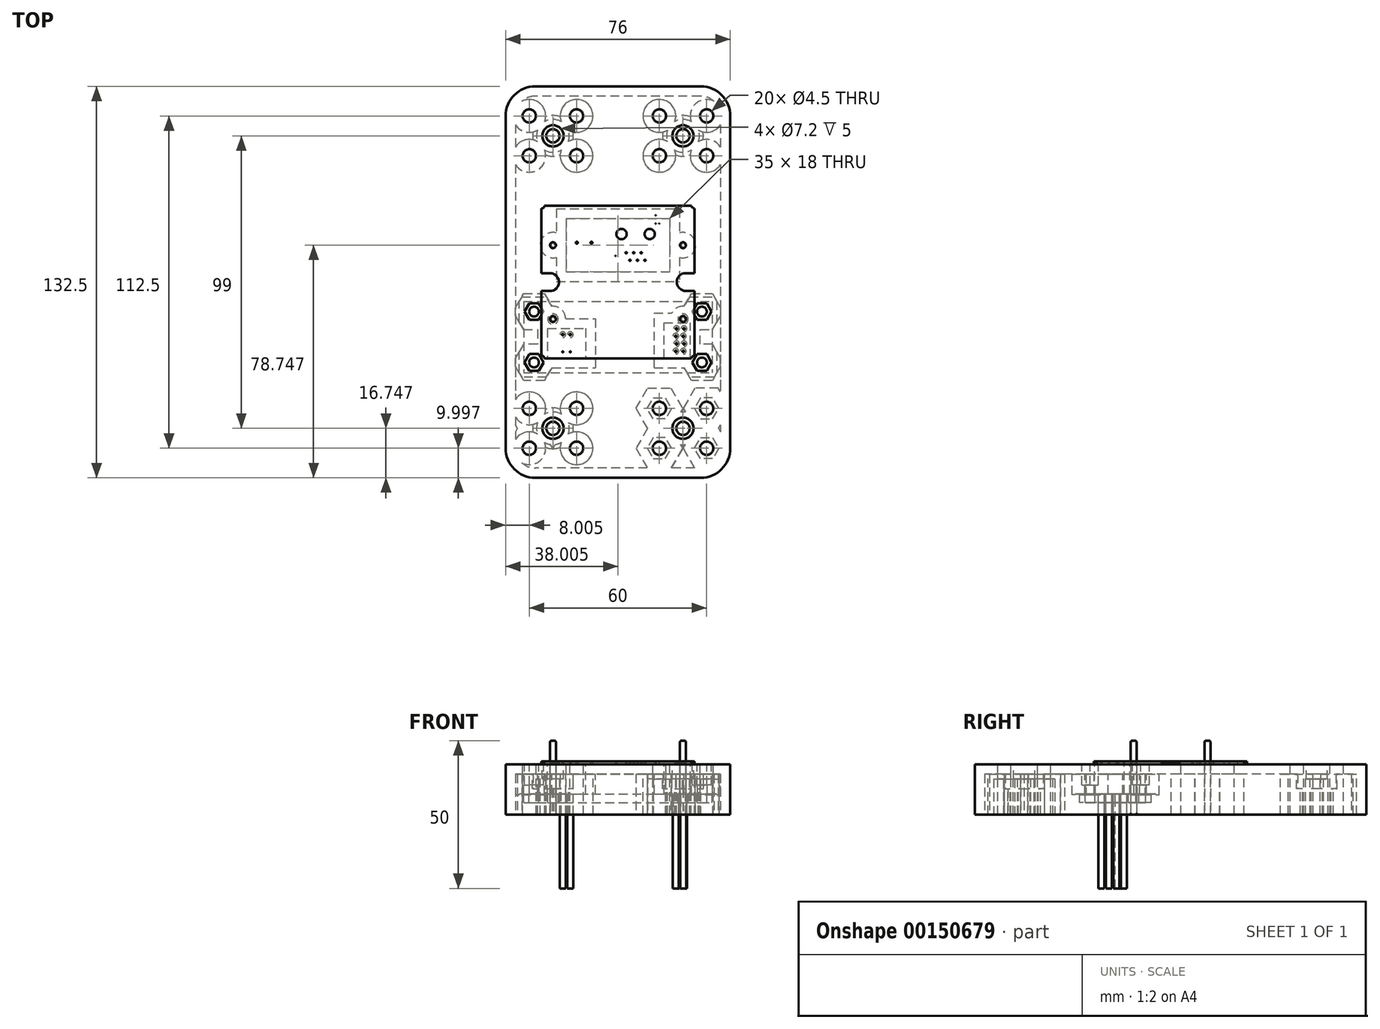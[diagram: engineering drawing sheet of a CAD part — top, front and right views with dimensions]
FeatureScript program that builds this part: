
annotation { "Feature Type Name" : "Feature", "Feature Type Description" : "" }
export const myFeature = defineFeature(function(context is Context, id is Id, definition is map)
    precondition{}
    {
        {
            var Q0;
            Q0=qCreatedBy(makeId("Top.planeOp"),FACE);
            var sketch = newSketch(context, id + "F0", { "sketchPlane" : qUnion([Q0])});
            skLineSegment(sketch, "E0", {"start": v(-14.15, 11.03) * mm, "end": v(-14.15, 0.89) * mm, "construction": true});
            skLineSegment(sketch, "E1", {"start": v(-14.15, 0.89) * mm, "end": v(-9.07, 0.89) * mm, "construction": true});
            skLineSegment(sketch, "E2", {"start": v(-9.07, 0.89) * mm, "end": v(-9.07, 11.03) * mm, "construction": true});
            skLineSegment(sketch, "E3", {"start": v(-9.07, 11.03) * mm, "end": v(-14.15, 11.03) * mm, "construction": true});
            skArc(sketch, "E4", {"start": v(-10.46, 10) * mm, "mid": v(-10.71, 9.75) * mm, "end": v(-10.46, 9.5) * mm});
            skArc(sketch, "E5", {"start": v(-10.46, 9.5) * mm, "mid": v(-10.21, 9.75) * mm, "end": v(-10.46, 10) * mm});
            skArc(sketch, "E6", {"start": v(-13, 10) * mm, "mid": v(-13.25, 9.75) * mm, "end": v(-13, 9.5) * mm});
            skArc(sketch, "E7", {"start": v(-13, 9.5) * mm, "mid": v(-12.75, 9.75) * mm, "end": v(-13, 10) * mm});
            skArc(sketch, "E8", {"start": v(-10.2, 7.46) * mm, "mid": v(-10.46, 7.2) * mm, "end": v(-10.2, 6.96) * mm});
            skArc(sketch, "E9", {"start": v(-10.2, 6.96) * mm, "mid": v(-9.96, 7.2) * mm, "end": v(-10.2, 7.46) * mm});
            skArc(sketch, "E10", {"start": v(-12.75, 7.46) * mm, "mid": v(-13, 7.2) * mm, "end": v(-12.75, 6.96) * mm});
            skArc(sketch, "E11", {"start": v(-12.75, 6.96) * mm, "mid": v(-12.5, 7.2) * mm, "end": v(-12.75, 7.46) * mm});
            skArc(sketch, "E12", {"start": v(-10.46, 4.42) * mm, "mid": v(-10.21, 4.67) * mm, "end": v(-10.46, 4.92) * mm});
            skArc(sketch, "E13", {"start": v(-10.46, 4.92) * mm, "mid": v(-10.71, 4.67) * mm, "end": v(-10.46, 4.42) * mm});
            skArc(sketch, "E14", {"start": v(-13, 4.92) * mm, "mid": v(-13.25, 4.67) * mm, "end": v(-13, 4.42) * mm});
            skArc(sketch, "E15", {"start": v(-13, 4.42) * mm, "mid": v(-12.75, 4.67) * mm, "end": v(-13, 4.92) * mm});
            skArc(sketch, "E16", {"start": v(-10.2, 2.38) * mm, "mid": v(-10.46, 2.13) * mm, "end": v(-10.2, 1.88) * mm});
            skArc(sketch, "E17", {"start": v(-10.2, 1.88) * mm, "mid": v(-9.96, 2.13) * mm, "end": v(-10.2, 2.38) * mm});
            skArc(sketch, "E18", {"start": v(-12.75, 2.38) * mm, "mid": v(-13, 2.13) * mm, "end": v(-12.75, 1.88) * mm});
            skArc(sketch, "E19", {"start": v(-12.75, 1.88) * mm, "mid": v(-12.5, 2.13) * mm, "end": v(-12.75, 2.38) * mm});
            skLineSegment(sketch, "E20", {"start": v(-49.07, -31) * mm, "end": v(-49.07, -23) * mm, "construction": true});
            skLineSegment(sketch, "E21", {"start": v(-49.07, -23) * mm, "end": v(-38.9, -23) * mm, "construction": true});
            skLineSegment(sketch, "E22", {"start": v(-38.9, -23) * mm, "end": v(-38.9, -31) * mm, "construction": true});
            skLineSegment(sketch, "E23", {"start": v(-38.9, -31) * mm, "end": v(-49.07, -31) * mm, "construction": true});
            skArc(sketch, "E24", {"start": v(-46.8, -27) * mm, "mid": v(-46.47, -27.32) * mm, "end": v(-46.15, -27) * mm});
            skArc(sketch, "E25", {"start": v(-46.15, -27) * mm, "mid": v(-46.47, -26.67) * mm, "end": v(-46.8, -27) * mm});
            skArc(sketch, "E26", {"start": v(-46.47, -25.92) * mm, "mid": v(-47.55, -27) * mm, "end": v(-46.47, -28.08) * mm, "construction": true});
            skArc(sketch, "E27", {"start": v(-46.47, -28.08) * mm, "mid": v(-45.4, -27) * mm, "end": v(-46.47, -25.92) * mm, "construction": true});
            skArc(sketch, "E28", {"start": v(-41.82, -27) * mm, "mid": v(-41.5, -27.32) * mm, "end": v(-41.17, -27) * mm});
            skArc(sketch, "E29", {"start": v(-41.17, -27) * mm, "mid": v(-41.5, -26.67) * mm, "end": v(-41.82, -27) * mm});
            skArc(sketch, "E30", {"start": v(-41.5, -25.92) * mm, "mid": v(-42.58, -27) * mm, "end": v(-41.5, -28.08) * mm, "construction": true});
            skArc(sketch, "E31", {"start": v(-41.5, -28.08) * mm, "mid": v(-40.42, -27) * mm, "end": v(-41.5, -25.92) * mm, "construction": true});
            skLineSegment(sketch, "E32", {"start": v(-47.67, 8.94) * mm, "end": v(-52.24, 8.94) * mm, "construction": true});
            skLineSegment(sketch, "E33", {"start": v(-52.24, 8.94) * mm, "end": v(-52.24, 10.97) * mm, "construction": true});
            skLineSegment(sketch, "E34", {"start": v(-52.24, 10.97) * mm, "end": v(-47.67, 10.97) * mm, "construction": true});
            skLineSegment(sketch, "E35", {"start": v(-47.67, 10.97) * mm, "end": v(-47.67, 8.94) * mm, "construction": true});
            skArc(sketch, "E36", {"start": v(-48.5, 9.96) * mm, "mid": v(-48.68, 10.13) * mm, "end": v(-48.86, 9.96) * mm});
            skArc(sketch, "E37", {"start": v(-48.86, 9.96) * mm, "mid": v(-48.68, 9.78) * mm, "end": v(-48.5, 9.96) * mm});
            skArc(sketch, "E38", {"start": v(-51.05, 9.96) * mm, "mid": v(-51.22, 10.13) * mm, "end": v(-51.4, 9.96) * mm});
            skArc(sketch, "E39", {"start": v(-51.4, 9.96) * mm, "mid": v(-51.22, 9.78) * mm, "end": v(-51.05, 9.96) * mm});
            skArc(sketch, "E40", {"start": v(-54.56, -0.55) * mm, "mid": v(-55.16, -1.16) * mm, "end": v(-54.56, -1.77) * mm});
            skArc(sketch, "E41", {"start": v(-54.56, -1.77) * mm, "mid": v(-53.95, -1.16) * mm, "end": v(-54.56, -0.55) * mm});
            skArc(sketch, "E42", {"start": v(-10.56, -1.77) * mm, "mid": v(-9.95, -1.16) * mm, "end": v(-10.56, -0.55) * mm});
            skArc(sketch, "E43", {"start": v(-10.56, -0.55) * mm, "mid": v(-11.16, -1.16) * mm, "end": v(-10.56, -1.77) * mm});
            skArc(sketch, "E44", {"start": v(-54.56, -26.77) * mm, "mid": v(-53.95, -26.16) * mm, "end": v(-54.56, -25.55) * mm});
            skArc(sketch, "E45", {"start": v(-54.56, -25.55) * mm, "mid": v(-55.16, -26.16) * mm, "end": v(-54.56, -26.77) * mm});
            skArc(sketch, "E46", {"start": v(-10.56, -26.77) * mm, "mid": v(-9.95, -26.16) * mm, "end": v(-10.56, -25.55) * mm});
            skArc(sketch, "E47", {"start": v(-10.56, -25.55) * mm, "mid": v(-11.16, -26.16) * mm, "end": v(-10.56, -26.77) * mm});
            skLineSegment(sketch, "E48", {"start": v(-19.8, -19.76) * mm, "end": v(-33.38, -19.76) * mm, "construction": true});
            skLineSegment(sketch, "E49", {"start": v(-33.38, -19.76) * mm, "end": v(-33.38, -36.27) * mm, "construction": true});
            skLineSegment(sketch, "E50", {"start": v(-33.38, -36.27) * mm, "end": v(-19.8, -36.27) * mm, "construction": true});
            skLineSegment(sketch, "E51", {"start": v(-19.8, -36.27) * mm, "end": v(-19.8, -19.76) * mm, "construction": true});
            skArc(sketch, "E52", {"start": v(-33.38, -36.24) * mm, "mid": v(-33.41, -36.27) * mm, "end": v(-33.38, -36.3) * mm, "construction": true});
            skArc(sketch, "E53", {"start": v(-33.38, -36.3) * mm, "mid": v(-33.35, -36.27) * mm, "end": v(-33.38, -36.24) * mm, "construction": true});
            skArc(sketch, "E54", {"start": v(-19.8, -36.24) * mm, "mid": v(-19.82, -36.27) * mm, "end": v(-19.8, -36.3) * mm});
            skArc(sketch, "E55", {"start": v(-19.8, -36.3) * mm, "mid": v(-19.76, -36.27) * mm, "end": v(-19.8, -36.24) * mm});
            skArc(sketch, "E56", {"start": v(-31.35, -28.16) * mm, "mid": v(-33.1, -29.92) * mm, "end": v(-31.35, -31.68) * mm});
            skArc(sketch, "E57", {"start": v(-31.35, -31.68) * mm, "mid": v(-29.6, -29.92) * mm, "end": v(-31.35, -28.16) * mm});
            skArc(sketch, "E58", {"start": v(-21.82, -28.19) * mm, "mid": v(-23.56, -29.92) * mm, "end": v(-21.82, -31.65) * mm});
            skArc(sketch, "E59", {"start": v(-21.82, -31.65) * mm, "mid": v(-20.1, -29.92) * mm, "end": v(-21.82, -28.19) * mm});
            skLineSegment(sketch, "E60", {"start": v(-33.38, -22.55) * mm, "end": v(-34.59, -22.55) * mm, "construction": true});
            skLineSegment(sketch, "E61", {"start": v(-34.59, -22.55) * mm, "end": v(-34.59, -33.48) * mm, "construction": true});
            skLineSegment(sketch, "E62", {"start": v(-34.59, -33.48) * mm, "end": v(-33.38, -33.48) * mm, "construction": true});
            skLineSegment(sketch, "E63", {"start": v(-33.38, -33.48) * mm, "end": v(-33.38, -22.55) * mm, "construction": true});
            skArc(sketch, "E64", {"start": v(-33.38, -22.52) * mm, "mid": v(-33.41, -22.55) * mm, "end": v(-33.38, -22.58) * mm});
            skArc(sketch, "E65", {"start": v(-33.38, -22.58) * mm, "mid": v(-33.35, -22.55) * mm, "end": v(-33.38, -22.52) * mm});
            skArc(sketch, "E66", {"start": v(-34.59, -33.44) * mm, "mid": v(-34.62, -33.48) * mm, "end": v(-34.59, -33.5) * mm, "construction": true});
            skArc(sketch, "E67", {"start": v(-34.59, -33.5) * mm, "mid": v(-34.56, -33.48) * mm, "end": v(-34.59, -33.44) * mm, "construction": true});
            skArc(sketch, "E68", {"start": v(-33.38, -33.44) * mm, "mid": v(-33.41, -33.48) * mm, "end": v(-33.38, -33.5) * mm, "construction": true});
            skArc(sketch, "E69", {"start": v(-33.38, -33.5) * mm, "mid": v(-33.35, -33.48) * mm, "end": v(-33.38, -33.44) * mm, "construction": true});
            skLineSegment(sketch, "E70", {"start": v(-19.8, -22.55) * mm, "end": v(-18.59, -22.55) * mm, "construction": true});
            skLineSegment(sketch, "E71", {"start": v(-18.59, -22.55) * mm, "end": v(-18.59, -33.48) * mm, "construction": true});
            skLineSegment(sketch, "E72", {"start": v(-18.59, -33.48) * mm, "end": v(-19.8, -33.48) * mm});
            skLineSegment(sketch, "E73", {"start": v(-19.8, -33.48) * mm, "end": v(-19.8, -22.55) * mm, "construction": true});
            skArc(sketch, "E74", {"start": v(-18.59, -33.44) * mm, "mid": v(-18.62, -33.48) * mm, "end": v(-18.59, -33.5) * mm});
            skArc(sketch, "E75", {"start": v(-18.59, -33.5) * mm, "mid": v(-18.55, -33.48) * mm, "end": v(-18.59, -33.44) * mm});
            skArc(sketch, "E76", {"start": v(-19.8, -33.44) * mm, "mid": v(-19.82, -33.48) * mm, "end": v(-19.8, -33.5) * mm});
            skArc(sketch, "E77", {"start": v(-19.8, -33.5) * mm, "mid": v(-19.76, -33.48) * mm, "end": v(-19.8, -33.44) * mm});
            skArc(sketch, "E78", {"start": v(-29.76, -23.34) * mm, "mid": v(-29.99, -23.57) * mm, "end": v(-29.76, -23.8) * mm});
            skArc(sketch, "E79", {"start": v(-29.76, -23.8) * mm, "mid": v(-29.54, -23.57) * mm, "end": v(-29.76, -23.34) * mm});
            skArc(sketch, "E80", {"start": v(-28.5, -21.25) * mm, "mid": v(-28.27, -21.03) * mm, "end": v(-28.5, -20.8) * mm});
            skArc(sketch, "E81", {"start": v(-28.5, -20.8) * mm, "mid": v(-28.72, -21.03) * mm, "end": v(-28.5, -21.25) * mm});
            skArc(sketch, "E82", {"start": v(-27.22, -23.34) * mm, "mid": v(-27.45, -23.57) * mm, "end": v(-27.22, -23.8) * mm});
            skArc(sketch, "E83", {"start": v(-27.22, -23.8) * mm, "mid": v(-27, -23.57) * mm, "end": v(-27.22, -23.34) * mm});
            skArc(sketch, "E84", {"start": v(-25.95, -21.25) * mm, "mid": v(-25.73, -21.03) * mm, "end": v(-25.95, -20.8) * mm});
            skArc(sketch, "E85", {"start": v(-25.95, -20.8) * mm, "mid": v(-26.18, -21.03) * mm, "end": v(-25.95, -21.25) * mm});
            skArc(sketch, "E86", {"start": v(-24.68, -23.34) * mm, "mid": v(-24.9, -23.57) * mm, "end": v(-24.68, -23.8) * mm});
            skArc(sketch, "E87", {"start": v(-24.68, -23.8) * mm, "mid": v(-24.46, -23.57) * mm, "end": v(-24.68, -23.34) * mm});
            skArc(sketch, "E88", {"start": v(-23.41, -21.25) * mm, "mid": v(-23.19, -21.03) * mm, "end": v(-23.41, -20.8) * mm});
            skArc(sketch, "E89", {"start": v(-23.41, -20.8) * mm, "mid": v(-23.64, -21.03) * mm, "end": v(-23.41, -21.25) * mm});
            skLineSegment(sketch, "E90", {"start": v(-52.5, 2.85) * mm, "end": v(-47.41, 2.85) * mm, "construction": true});
            skLineSegment(sketch, "E91", {"start": v(-47.41, 2.85) * mm, "end": v(-47.41, 5.39) * mm, "construction": true});
            skLineSegment(sketch, "E92", {"start": v(-47.41, 5.39) * mm, "end": v(-52.5, 5.39) * mm, "construction": true});
            skLineSegment(sketch, "E93", {"start": v(-52.5, 5.39) * mm, "end": v(-52.5, 2.85) * mm, "construction": true});
            skArc(sketch, "E94", {"start": v(-51.47, 4.12) * mm, "mid": v(-51.22, 3.87) * mm, "end": v(-50.97, 4.12) * mm});
            skArc(sketch, "E95", {"start": v(-50.97, 4.12) * mm, "mid": v(-51.22, 4.37) * mm, "end": v(-51.47, 4.12) * mm});
            skArc(sketch, "E96", {"start": v(-48.93, 4.12) * mm, "mid": v(-48.68, 3.87) * mm, "end": v(-48.43, 4.12) * mm});
            skArc(sketch, "E97", {"start": v(-48.43, 4.12) * mm, "mid": v(-48.68, 4.37) * mm, "end": v(-48.93, 4.12) * mm});
            skArc(sketch, "E98", {"start": v(-58.48, -38.56) * mm, "mid": v(-58.46, -38.59) * mm, "end": v(-58.43, -38.56) * mm});
            skArc(sketch, "E99", {"start": v(-58.43, -38.56) * mm, "mid": v(-58.46, -38.54) * mm, "end": v(-58.48, -38.56) * mm});
            skArc(sketch, "E100", {"start": v(-54.42, -16.46) * mm, "mid": v(-54.4, -16.48) * mm, "end": v(-54.37, -16.46) * mm});
            skArc(sketch, "E101", {"start": v(-54.37, -16.46) * mm, "mid": v(-54.4, -16.43) * mm, "end": v(-54.42, -16.46) * mm});
            skArc(sketch, "E102", {"start": v(-53.92, -16.2) * mm, "mid": v(-53.9, -16.23) * mm, "end": v(-53.87, -16.2) * mm});
            skArc(sketch, "E103", {"start": v(-53.87, -16.2) * mm, "mid": v(-53.9, -16.18) * mm, "end": v(-53.92, -16.2) * mm});
            skArc(sketch, "E104", {"start": v(-53.33, -15.7) * mm, "mid": v(-53.3, -15.72) * mm, "end": v(-53.28, -15.7) * mm});
            skArc(sketch, "E105", {"start": v(-53.28, -15.7) * mm, "mid": v(-53.3, -15.67) * mm, "end": v(-53.33, -15.7) * mm});
            skArc(sketch, "E106", {"start": v(-52.98, -15.19) * mm, "mid": v(-52.95, -15.21) * mm, "end": v(-52.93, -15.19) * mm});
            skArc(sketch, "E107", {"start": v(-52.93, -15.19) * mm, "mid": v(-52.95, -15.16) * mm, "end": v(-52.98, -15.19) * mm});
            skArc(sketch, "E108", {"start": v(-52.72, -14.68) * mm, "mid": v(-52.7, -14.7) * mm, "end": v(-52.67, -14.68) * mm});
            skArc(sketch, "E109", {"start": v(-52.67, -14.68) * mm, "mid": v(-52.7, -14.65) * mm, "end": v(-52.72, -14.68) * mm});
            skArc(sketch, "E110", {"start": v(-52.6, -14.17) * mm, "mid": v(-52.57, -14.2) * mm, "end": v(-52.55, -14.17) * mm});
            skArc(sketch, "E111", {"start": v(-52.55, -14.17) * mm, "mid": v(-52.57, -14.15) * mm, "end": v(-52.6, -14.17) * mm});
            skArc(sketch, "E112", {"start": v(-52.54, -13.66) * mm, "mid": v(-52.52, -13.69) * mm, "end": v(-52.5, -13.66) * mm});
            skArc(sketch, "E113", {"start": v(-52.5, -13.66) * mm, "mid": v(-52.52, -13.64) * mm, "end": v(-52.54, -13.66) * mm});
            skArc(sketch, "E114", {"start": v(-52.6, -13.16) * mm, "mid": v(-52.57, -13.18) * mm, "end": v(-52.55, -13.16) * mm});
            skArc(sketch, "E115", {"start": v(-52.55, -13.16) * mm, "mid": v(-52.57, -13.13) * mm, "end": v(-52.6, -13.16) * mm});
            skArc(sketch, "E116", {"start": v(-52.72, -12.65) * mm, "mid": v(-52.7, -12.67) * mm, "end": v(-52.67, -12.65) * mm});
            skArc(sketch, "E117", {"start": v(-52.67, -12.65) * mm, "mid": v(-52.7, -12.62) * mm, "end": v(-52.72, -12.65) * mm});
            skArc(sketch, "E118", {"start": v(-52.98, -12.14) * mm, "mid": v(-52.95, -12.16) * mm, "end": v(-52.93, -12.14) * mm});
            skArc(sketch, "E119", {"start": v(-52.93, -12.14) * mm, "mid": v(-52.95, -12.11) * mm, "end": v(-52.98, -12.14) * mm});
            skArc(sketch, "E120", {"start": v(-53.3, -11.63) * mm, "mid": v(-53.28, -11.66) * mm, "end": v(-53.26, -11.63) * mm});
            skArc(sketch, "E121", {"start": v(-53.26, -11.63) * mm, "mid": v(-53.28, -11.6) * mm, "end": v(-53.3, -11.63) * mm});
            skArc(sketch, "E122", {"start": v(-53.94, -11.12) * mm, "mid": v(-53.92, -11.15) * mm, "end": v(-53.9, -11.12) * mm});
            skArc(sketch, "E123", {"start": v(-53.9, -11.12) * mm, "mid": v(-53.92, -11.1) * mm, "end": v(-53.94, -11.12) * mm});
            skArc(sketch, "E124", {"start": v(-54.5, -10.84) * mm, "mid": v(-54.48, -10.87) * mm, "end": v(-54.45, -10.84) * mm});
            skArc(sketch, "E125", {"start": v(-54.45, -10.84) * mm, "mid": v(-54.48, -10.82) * mm, "end": v(-54.5, -10.84) * mm});
            skArc(sketch, "E126", {"start": v(-55.11, -10.7) * mm, "mid": v(-55.09, -10.72) * mm, "end": v(-55.06, -10.7) * mm});
            skArc(sketch, "E127", {"start": v(-55.06, -10.7) * mm, "mid": v(-55.09, -10.67) * mm, "end": v(-55.11, -10.7) * mm});
            skArc(sketch, "E128", {"start": v(-55.57, -10.66) * mm, "mid": v(-55.54, -10.69) * mm, "end": v(-55.52, -10.66) * mm});
            skArc(sketch, "E129", {"start": v(-55.52, -10.66) * mm, "mid": v(-55.54, -10.64) * mm, "end": v(-55.57, -10.66) * mm});
            skArc(sketch, "E130", {"start": v(-58.48, 11.24) * mm, "mid": v(-58.46, 11.21) * mm, "end": v(-58.43, 11.24) * mm});
            skArc(sketch, "E131", {"start": v(-58.43, 11.24) * mm, "mid": v(-58.46, 11.26) * mm, "end": v(-58.48, 11.24) * mm});
            skArc(sketch, "E132", {"start": v(-58.44, 11.24) * mm, "mid": v(-58.42, 11.21) * mm, "end": v(-58.4, 11.24) * mm});
            skArc(sketch, "E133", {"start": v(-58.4, 11.24) * mm, "mid": v(-58.42, 11.26) * mm, "end": v(-58.44, 11.24) * mm});
            skArc(sketch, "E134", {"start": v(-58.4, 11.24) * mm, "mid": v(-58.37, 11.22) * mm, "end": v(-58.34, 11.24) * mm});
            skArc(sketch, "E135", {"start": v(-58.34, 11.24) * mm, "mid": v(-58.37, 11.27) * mm, "end": v(-58.4, 11.24) * mm});
            skArc(sketch, "E136", {"start": v(-58.24, 11.26) * mm, "mid": v(-58.22, 11.24) * mm, "end": v(-58.2, 11.26) * mm});
            skArc(sketch, "E137", {"start": v(-58.2, 11.26) * mm, "mid": v(-58.22, 11.29) * mm, "end": v(-58.24, 11.26) * mm});
            skArc(sketch, "E138", {"start": v(-58.2, 11.28) * mm, "mid": v(-58.17, 11.25) * mm, "end": v(-58.14, 11.28) * mm});
            skArc(sketch, "E139", {"start": v(-58.14, 11.28) * mm, "mid": v(-58.17, 11.3) * mm, "end": v(-58.2, 11.28) * mm});
            skArc(sketch, "E140", {"start": v(-58.1, 11.3) * mm, "mid": v(-58.08, 11.28) * mm, "end": v(-58.06, 11.3) * mm});
            skArc(sketch, "E141", {"start": v(-58.06, 11.3) * mm, "mid": v(-58.08, 11.33) * mm, "end": v(-58.1, 11.3) * mm});
            skArc(sketch, "E142", {"start": v(-58, 11.36) * mm, "mid": v(-57.98, 11.33) * mm, "end": v(-57.95, 11.36) * mm});
            skArc(sketch, "E143", {"start": v(-57.95, 11.36) * mm, "mid": v(-57.98, 11.38) * mm, "end": v(-58, 11.36) * mm});
            skArc(sketch, "E144", {"start": v(-57.95, 11.39) * mm, "mid": v(-57.92, 11.36) * mm, "end": v(-57.9, 11.39) * mm});
            skArc(sketch, "E145", {"start": v(-57.9, 11.39) * mm, "mid": v(-57.92, 11.41) * mm, "end": v(-57.95, 11.39) * mm});
            skArc(sketch, "E146", {"start": v(-57.9, 11.42) * mm, "mid": v(-57.87, 11.4) * mm, "end": v(-57.85, 11.42) * mm});
            skArc(sketch, "E147", {"start": v(-57.85, 11.42) * mm, "mid": v(-57.87, 11.45) * mm, "end": v(-57.9, 11.42) * mm});
            skArc(sketch, "E148", {"start": v(-57.81, 11.5) * mm, "mid": v(-57.79, 11.47) * mm, "end": v(-57.76, 11.5) * mm});
            skArc(sketch, "E149", {"start": v(-57.76, 11.5) * mm, "mid": v(-57.79, 11.52) * mm, "end": v(-57.81, 11.5) * mm});
            skArc(sketch, "E150", {"start": v(-57.74, 11.56) * mm, "mid": v(-57.72, 11.54) * mm, "end": v(-57.7, 11.56) * mm});
            skArc(sketch, "E151", {"start": v(-57.7, 11.56) * mm, "mid": v(-57.72, 11.59) * mm, "end": v(-57.74, 11.56) * mm});
            skArc(sketch, "E152", {"start": v(-57.68, 11.64) * mm, "mid": v(-57.65, 11.61) * mm, "end": v(-57.63, 11.64) * mm});
            skArc(sketch, "E153", {"start": v(-57.63, 11.64) * mm, "mid": v(-57.65, 11.66) * mm, "end": v(-57.68, 11.64) * mm});
            skArc(sketch, "E154", {"start": v(-57.63, 11.7) * mm, "mid": v(-57.6, 11.68) * mm, "end": v(-57.58, 11.7) * mm});
            skArc(sketch, "E155", {"start": v(-57.58, 11.7) * mm, "mid": v(-57.6, 11.73) * mm, "end": v(-57.63, 11.7) * mm});
            skArc(sketch, "E156", {"start": v(-57.62, 11.73) * mm, "mid": v(-57.6, 11.7) * mm, "end": v(-57.57, 11.73) * mm});
            skArc(sketch, "E157", {"start": v(-57.57, 11.73) * mm, "mid": v(-57.6, 11.76) * mm, "end": v(-57.62, 11.73) * mm});
            skLineSegment(sketch, "E158", {"start": v(-58.46, -38.56) * mm, "end": v(-58.46, -16.66) * mm});
            skLineSegment(sketch, "E159", {"start": v(-58.46, -16.66) * mm, "end": v(-55.47, -16.66) * mm});
            skLineSegment(sketch, "E160", {"start": v(-55.47, -16.66) * mm, "end": v(-54.93, -16.6) * mm});
            skLineSegment(sketch, "E161", {"start": v(-54.93, -16.6) * mm, "end": v(-54.4, -16.46) * mm});
            skLineSegment(sketch, "E162", {"start": v(-54.4, -16.46) * mm, "end": v(-53.9, -16.2) * mm});
            skLineSegment(sketch, "E163", {"start": v(-53.9, -16.2) * mm, "end": v(-53.3, -15.7) * mm});
            skLineSegment(sketch, "E164", {"start": v(-53.3, -15.7) * mm, "end": v(-52.95, -15.19) * mm});
            skLineSegment(sketch, "E165", {"start": v(-52.95, -15.19) * mm, "end": v(-52.7, -14.68) * mm});
            skLineSegment(sketch, "E166", {"start": v(-52.7, -14.68) * mm, "end": v(-52.57, -14.17) * mm});
            skLineSegment(sketch, "E167", {"start": v(-52.57, -14.17) * mm, "end": v(-52.52, -13.66) * mm});
            skLineSegment(sketch, "E168", {"start": v(-52.52, -13.66) * mm, "end": v(-52.57, -13.16) * mm});
            skLineSegment(sketch, "E169", {"start": v(-52.57, -13.16) * mm, "end": v(-52.7, -12.65) * mm});
            skLineSegment(sketch, "E170", {"start": v(-52.7, -12.65) * mm, "end": v(-52.95, -12.14) * mm});
            skLineSegment(sketch, "E171", {"start": v(-52.95, -12.14) * mm, "end": v(-53.28, -11.63) * mm});
            skLineSegment(sketch, "E172", {"start": v(-53.28, -11.63) * mm, "end": v(-53.92, -11.12) * mm});
            skLineSegment(sketch, "E173", {"start": v(-53.92, -11.12) * mm, "end": v(-54.48, -10.84) * mm});
            skLineSegment(sketch, "E174", {"start": v(-54.48, -10.84) * mm, "end": v(-55.09, -10.7) * mm});
            skLineSegment(sketch, "E175", {"start": v(-55.09, -10.7) * mm, "end": v(-55.54, -10.66) * mm});
            skLineSegment(sketch, "E176", {"start": v(-55.54, -10.66) * mm, "end": v(-58.46, -10.66) * mm});
            skLineSegment(sketch, "E177", {"start": v(-58.46, -10.66) * mm, "end": v(-58.46, 11.24) * mm});
            skLineSegment(sketch, "E178", {"start": v(-58.46, 11.24) * mm, "end": v(-58.42, 11.24) * mm});
            skLineSegment(sketch, "E179", {"start": v(-58.42, 11.24) * mm, "end": v(-58.37, 11.24) * mm});
            skLineSegment(sketch, "E180", {"start": v(-58.37, 11.24) * mm, "end": v(-58.22, 11.26) * mm});
            skLineSegment(sketch, "E181", {"start": v(-58.22, 11.26) * mm, "end": v(-58.17, 11.28) * mm});
            skLineSegment(sketch, "E182", {"start": v(-58.17, 11.28) * mm, "end": v(-58.08, 11.3) * mm});
            skLineSegment(sketch, "E183", {"start": v(-58.08, 11.3) * mm, "end": v(-57.98, 11.36) * mm});
            skLineSegment(sketch, "E184", {"start": v(-57.98, 11.36) * mm, "end": v(-57.92, 11.39) * mm});
            skLineSegment(sketch, "E185", {"start": v(-57.92, 11.39) * mm, "end": v(-57.87, 11.42) * mm});
            skLineSegment(sketch, "E186", {"start": v(-57.87, 11.42) * mm, "end": v(-57.79, 11.5) * mm});
            skLineSegment(sketch, "E187", {"start": v(-57.79, 11.5) * mm, "end": v(-57.72, 11.56) * mm});
            skLineSegment(sketch, "E188", {"start": v(-57.72, 11.56) * mm, "end": v(-57.65, 11.64) * mm});
            skLineSegment(sketch, "E189", {"start": v(-57.65, 11.64) * mm, "end": v(-57.6, 11.7) * mm});
            skLineSegment(sketch, "E190", {"start": v(-57.6, 11.7) * mm, "end": v(-57.6, 11.73) * mm});
            skLineSegment(sketch, "E191", {"start": v(-57.6, 11.73) * mm, "end": v(-57.57, 11.77) * mm});
            skLineSegment(sketch, "E192", {"start": v(-57.57, 11.77) * mm, "end": v(-57.52, 11.88) * mm});
            skLineSegment(sketch, "E193", {"start": v(-57.52, 11.88) * mm, "end": v(-57.51, 11.9) * mm});
            skLineSegment(sketch, "E194", {"start": v(-57.51, 11.9) * mm, "end": v(-57.5, 11.94) * mm});
            skLineSegment(sketch, "E195", {"start": v(-57.5, 11.94) * mm, "end": v(-57.49, 11.98) * mm});
            skLineSegment(sketch, "E196", {"start": v(-57.49, 11.98) * mm, "end": v(-57.46, 12.15) * mm});
            skLineSegment(sketch, "E197", {"start": v(-57.46, 12.15) * mm, "end": v(-57.46, 12.2) * mm});
            skLineSegment(sketch, "E198", {"start": v(-57.46, 12.2) * mm, "end": v(-57.46, 12.24) * mm});
            skLineSegment(sketch, "E199", {"start": v(-57.46, 12.24) * mm, "end": v(-7.66, 12.24) * mm});
            skLineSegment(sketch, "E200", {"start": v(-7.66, 12.24) * mm, "end": v(-7.66, 12.22) * mm});
            skLineSegment(sketch, "E201", {"start": v(-7.66, 12.22) * mm, "end": v(-7.64, 12.09) * mm});
            skLineSegment(sketch, "E202", {"start": v(-7.64, 12.09) * mm, "end": v(-7.63, 12.02) * mm});
            skLineSegment(sketch, "E203", {"start": v(-7.63, 12.02) * mm, "end": v(-7.58, 11.85) * mm});
            skLineSegment(sketch, "E204", {"start": v(-7.58, 11.85) * mm, "end": v(-7.54, 11.76) * mm});
            skLineSegment(sketch, "E205", {"start": v(-7.54, 11.76) * mm, "end": v(-7.43, 11.6) * mm});
            skLineSegment(sketch, "E206", {"start": v(-7.43, 11.6) * mm, "end": v(-7.28, 11.46) * mm});
            skLineSegment(sketch, "E207", {"start": v(-7.28, 11.46) * mm, "end": v(-7.11, 11.35) * mm});
            skLineSegment(sketch, "E208", {"start": v(-7.11, 11.35) * mm, "end": v(-6.94, 11.28) * mm});
            skLineSegment(sketch, "E209", {"start": v(-6.94, 11.28) * mm, "end": v(-6.75, 11.24) * mm});
            skLineSegment(sketch, "E210", {"start": v(-6.75, 11.24) * mm, "end": v(-6.67, 11.24) * mm});
            skLineSegment(sketch, "E211", {"start": v(-6.67, 11.24) * mm, "end": v(-6.66, 11.24) * mm});
            skLineSegment(sketch, "E212", {"start": v(-6.66, 11.24) * mm, "end": v(-6.66, -10.66) * mm});
            skLineSegment(sketch, "E213", {"start": v(-6.66, -10.66) * mm, "end": v(-9.64, -10.66) * mm});
            skLineSegment(sketch, "E214", {"start": v(-9.64, -10.66) * mm, "end": v(-10.23, -10.7) * mm});
            skLineSegment(sketch, "E215", {"start": v(-10.23, -10.7) * mm, "end": v(-10.76, -10.87) * mm});
            skLineSegment(sketch, "E216", {"start": v(-10.76, -10.87) * mm, "end": v(-11.24, -11.12) * mm});
            skLineSegment(sketch, "E217", {"start": v(-11.24, -11.12) * mm, "end": v(-11.85, -11.63) * mm});
            skLineSegment(sketch, "E218", {"start": v(-11.85, -11.63) * mm, "end": v(-12.2, -12.14) * mm});
            skLineSegment(sketch, "E219", {"start": v(-12.2, -12.14) * mm, "end": v(-12.44, -12.65) * mm});
            skLineSegment(sketch, "E220", {"start": v(-12.44, -12.65) * mm, "end": v(-12.6, -13.16) * mm});
            skLineSegment(sketch, "E221", {"start": v(-12.6, -13.16) * mm, "end": v(-12.62, -13.66) * mm});
            skLineSegment(sketch, "E222", {"start": v(-12.62, -13.66) * mm, "end": v(-12.6, -14.17) * mm});
            skLineSegment(sketch, "E223", {"start": v(-12.6, -14.17) * mm, "end": v(-12.44, -14.68) * mm});
            skLineSegment(sketch, "E224", {"start": v(-12.44, -14.68) * mm, "end": v(-12.2, -15.19) * mm});
            skLineSegment(sketch, "E225", {"start": v(-12.2, -15.19) * mm, "end": v(-11.85, -15.7) * mm});
            skLineSegment(sketch, "E226", {"start": v(-11.85, -15.7) * mm, "end": v(-11.27, -16.2) * mm});
            skLineSegment(sketch, "E227", {"start": v(-11.27, -16.2) * mm, "end": v(-10.81, -16.46) * mm});
            skLineSegment(sketch, "E228", {"start": v(-10.81, -16.46) * mm, "end": v(-10.2, -16.63) * mm});
            skLineSegment(sketch, "E229", {"start": v(-10.2, -16.63) * mm, "end": v(-9.64, -16.66) * mm});
            skLineSegment(sketch, "E230", {"start": v(-9.64, -16.66) * mm, "end": v(-6.66, -16.66) * mm});
            skLineSegment(sketch, "E231", {"start": v(-6.66, -16.66) * mm, "end": v(-6.66, -38.56) * mm});
            skLineSegment(sketch, "E232", {"start": v(-6.66, -38.56) * mm, "end": v(-6.9, -38.6) * mm});
            skLineSegment(sketch, "E233", {"start": v(-6.9, -38.6) * mm, "end": v(-7.12, -38.68) * mm});
            skLineSegment(sketch, "E234", {"start": v(-7.12, -38.68) * mm, "end": v(-7.33, -38.82) * mm});
            skLineSegment(sketch, "E235", {"start": v(-7.33, -38.82) * mm, "end": v(-7.48, -39) * mm});
            skLineSegment(sketch, "E236", {"start": v(-7.48, -39) * mm, "end": v(-7.56, -39.15) * mm});
            skLineSegment(sketch, "E237", {"start": v(-7.56, -39.15) * mm, "end": v(-7.62, -39.3) * mm});
            skLineSegment(sketch, "E238", {"start": v(-7.62, -39.3) * mm, "end": v(-7.65, -39.43) * mm});
            skLineSegment(sketch, "E239", {"start": v(-7.65, -39.43) * mm, "end": v(-7.66, -39.56) * mm});
            skLineSegment(sketch, "E240", {"start": v(-7.66, -39.56) * mm, "end": v(-57.46, -39.56) * mm});
            skLineSegment(sketch, "E241", {"start": v(-57.46, -39.56) * mm, "end": v(-57.47, -39.4) * mm});
            skLineSegment(sketch, "E242", {"start": v(-57.47, -39.4) * mm, "end": v(-57.5, -39.25) * mm});
            skLineSegment(sketch, "E243", {"start": v(-57.5, -39.25) * mm, "end": v(-57.6, -39.05) * mm});
            skLineSegment(sketch, "E244", {"start": v(-57.6, -39.05) * mm, "end": v(-57.71, -38.9) * mm});
            skLineSegment(sketch, "E245", {"start": v(-57.71, -38.9) * mm, "end": v(-57.85, -38.77) * mm});
            skLineSegment(sketch, "E246", {"start": v(-57.85, -38.77) * mm, "end": v(-58, -38.67) * mm});
            skLineSegment(sketch, "E247", {"start": v(-58, -38.67) * mm, "end": v(-58.12, -38.62) * mm});
            skLineSegment(sketch, "E248", {"start": v(-58.12, -38.62) * mm, "end": v(-58.25, -38.59) * mm});
            skLineSegment(sketch, "E249", {"start": v(-58.25, -38.59) * mm, "end": v(-58.37, -38.57) * mm});
            skLineSegment(sketch, "E250", {"start": v(-58.37, -38.57) * mm, "end": v(-58.46, -38.56) * mm});
            skArc(sketch, "E251.MirrorCS", {"start": v(-58.06, 13.16) * mm, "mid": v(-58.08, 13.14) * mm, "end": v(-58.1, 13.16) * mm});
            skArc(sketch, "E252.MirrorCS", {"start": v(-58, 13.12) * mm, "mid": v(-57.98, 13.14) * mm, "end": v(-57.95, 13.12) * mm});
            skArc(sketch, "E253.MirrorCS", {"start": v(-57.95, 13.12) * mm, "mid": v(-57.98, 13.1) * mm, "end": v(-58, 13.12) * mm});
            skArc(sketch, "E254.MirrorCS", {"start": v(-57.95, 13.08) * mm, "mid": v(-57.92, 13.1) * mm, "end": v(-57.9, 13.08) * mm});
            skArc(sketch, "E255.MirrorCS", {"start": v(-57.9, 13.08) * mm, "mid": v(-57.92, 13.06) * mm, "end": v(-57.95, 13.08) * mm});
            skArc(sketch, "E256.MirrorCS", {"start": v(-57.9, 13.05) * mm, "mid": v(-57.87, 13.07) * mm, "end": v(-57.85, 13.05) * mm});
            skArc(sketch, "E257.MirrorCS", {"start": v(-58.48, 13.24) * mm, "mid": v(-58.46, 13.26) * mm, "end": v(-58.43, 13.24) * mm});
            skArc(sketch, "E258.MirrorCS", {"start": v(-57.85, 13.05) * mm, "mid": v(-57.87, 13.02) * mm, "end": v(-57.9, 13.05) * mm});
            skLineSegment(sketch, "E259.MirrorCS", {"start": v(-58.46, 13.24) * mm, "end": v(-58.42, 13.24) * mm});
            skArc(sketch, "E260.MirrorCS", {"start": v(-57.81, 12.98) * mm, "mid": v(-57.79, 13) * mm, "end": v(-57.76, 12.98) * mm});
            skArc(sketch, "E261.MirrorCS", {"start": v(-58.43, 13.24) * mm, "mid": v(-58.46, 13.21) * mm, "end": v(-58.48, 13.24) * mm});
            skArc(sketch, "E262.MirrorCS", {"start": v(-57.76, 12.98) * mm, "mid": v(-57.79, 12.96) * mm, "end": v(-57.81, 12.98) * mm});
            skLineSegment(sketch, "E263.MirrorCS", {"start": v(-58.42, 13.24) * mm, "end": v(-58.37, 13.23) * mm});
            skArc(sketch, "E264.MirrorCS", {"start": v(-57.74, 12.9) * mm, "mid": v(-57.72, 12.93) * mm, "end": v(-57.7, 12.9) * mm});
            skArc(sketch, "E265.MirrorCS", {"start": v(-58.44, 13.24) * mm, "mid": v(-58.42, 13.26) * mm, "end": v(-58.4, 13.24) * mm});
            skLineSegment(sketch, "E266.MirrorCS", {"start": v(-58.08, 13.16) * mm, "end": v(-57.98, 13.12) * mm});
            skLineSegment(sketch, "E267.MirrorCS", {"start": v(-58.37, 13.23) * mm, "end": v(-58.22, 13.2) * mm});
            skArc(sketch, "E268.MirrorCS", {"start": v(-57.7, 12.9) * mm, "mid": v(-57.72, 12.88) * mm, "end": v(-57.74, 12.9) * mm});
            skArc(sketch, "E269.MirrorCS", {"start": v(-58.4, 13.24) * mm, "mid": v(-58.42, 13.21) * mm, "end": v(-58.44, 13.24) * mm});
            skLineSegment(sketch, "E270.MirrorCS", {"start": v(-57.98, 13.12) * mm, "end": v(-57.92, 13.08) * mm});
            skLineSegment(sketch, "E271.MirrorCS", {"start": v(-58.22, 13.2) * mm, "end": v(-58.17, 13.2) * mm});
            skArc(sketch, "E272.MirrorCS", {"start": v(-57.68, 12.84) * mm, "mid": v(-57.65, 12.86) * mm, "end": v(-57.63, 12.84) * mm});
            skArc(sketch, "E273.MirrorCS", {"start": v(-57.57, 12.74) * mm, "mid": v(-57.6, 12.72) * mm, "end": v(-57.62, 12.74) * mm});
            skArc(sketch, "E274.MirrorCS", {"start": v(-58.4, 13.23) * mm, "mid": v(-58.37, 13.26) * mm, "end": v(-58.34, 13.23) * mm});
            skLineSegment(sketch, "E275.MirrorCS", {"start": v(-57.92, 13.08) * mm, "end": v(-57.87, 13.05) * mm});
            skLineSegment(sketch, "E276.MirrorCS", {"start": v(-57.6, 12.77) * mm, "end": v(-57.6, 12.74) * mm});
            skLineSegment(sketch, "E277.MirrorCS", {"start": v(-58.17, 13.2) * mm, "end": v(-58.08, 13.16) * mm});
            skArc(sketch, "E278.MirrorCS", {"start": v(-57.63, 12.84) * mm, "mid": v(-57.65, 12.81) * mm, "end": v(-57.68, 12.84) * mm});
            skLineSegment(sketch, "E279.MirrorCS", {"start": v(-57.6, 12.74) * mm, "end": v(-57.57, 12.7) * mm});
            skLineSegment(sketch, "E280.MirrorCS", {"start": v(-57.51, 12.56) * mm, "end": v(-57.5, 12.53) * mm});
            skArc(sketch, "E281.MirrorCS", {"start": v(-58.34, 13.23) * mm, "mid": v(-58.37, 13.2) * mm, "end": v(-58.4, 13.23) * mm});
            skLineSegment(sketch, "E282.MirrorCS", {"start": v(-57.87, 13.05) * mm, "end": v(-57.79, 12.98) * mm});
            skLineSegment(sketch, "E283.MirrorCS", {"start": v(-57.57, 12.7) * mm, "end": v(-57.52, 12.6) * mm});
            skLineSegment(sketch, "E284.MirrorCS", {"start": v(-57.5, 12.53) * mm, "end": v(-57.49, 12.5) * mm});
            skArc(sketch, "E285.MirrorCS", {"start": v(-58.24, 13.2) * mm, "mid": v(-58.22, 13.23) * mm, "end": v(-58.2, 13.2) * mm});
            skArc(sketch, "E286.MirrorCS", {"start": v(-57.63, 12.77) * mm, "mid": v(-57.6, 12.8) * mm, "end": v(-57.58, 12.77) * mm});
            skLineSegment(sketch, "E287.MirrorCS", {"start": v(-57.52, 12.6) * mm, "end": v(-57.51, 12.56) * mm});
            skLineSegment(sketch, "E288.MirrorCS", {"start": v(-57.49, 12.5) * mm, "end": v(-57.46, 12.32) * mm});
            skArc(sketch, "E289.MirrorCS", {"start": v(-58.2, 13.2) * mm, "mid": v(-58.22, 13.18) * mm, "end": v(-58.24, 13.2) * mm});
            skLineSegment(sketch, "E290.MirrorCS", {"start": v(-57.79, 12.98) * mm, "end": v(-57.72, 12.9) * mm});
            skLineSegment(sketch, "E291.MirrorCS", {"start": v(-57.46, 12.32) * mm, "end": v(-57.46, 12.28) * mm});
            skArc(sketch, "E292.MirrorCS", {"start": v(-58.2, 13.2) * mm, "mid": v(-58.17, 13.22) * mm, "end": v(-58.14, 13.2) * mm});
            skArc(sketch, "E293.MirrorCS", {"start": v(-57.58, 12.77) * mm, "mid": v(-57.6, 12.75) * mm, "end": v(-57.63, 12.77) * mm});
            skLineSegment(sketch, "E294.MirrorCS", {"start": v(-57.72, 12.9) * mm, "end": v(-57.65, 12.84) * mm});
            skLineSegment(sketch, "E295.MirrorCS", {"start": v(-57.65, 12.84) * mm, "end": v(-57.6, 12.77) * mm});
            skLineSegment(sketch, "E296.MirrorCS", {"start": v(-57.46, 12.28) * mm, "end": v(-57.46, 12.24) * mm});
            skArc(sketch, "E297.MirrorCS", {"start": v(-58.14, 13.2) * mm, "mid": v(-58.17, 13.17) * mm, "end": v(-58.2, 13.2) * mm});
            skArc(sketch, "E298.MirrorCS", {"start": v(-57.62, 12.74) * mm, "mid": v(-57.6, 12.77) * mm, "end": v(-57.57, 12.74) * mm});
            skArc(sketch, "E299.MirrorCS", {"start": v(-58.1, 13.16) * mm, "mid": v(-58.08, 13.19) * mm, "end": v(-58.06, 13.16) * mm});
            skArc(sketch, "E300.MirrorCS", {"start": v(-52.67, 39.15) * mm, "mid": v(-52.7, 39.13) * mm, "end": v(-52.72, 39.15) * mm});
            skArc(sketch, "E301.MirrorCS", {"start": v(-52.72, 37.12) * mm, "mid": v(-52.7, 37.15) * mm, "end": v(-52.67, 37.12) * mm});
            skArc(sketch, "E302.MirrorCS", {"start": v(-52.6, 38.64) * mm, "mid": v(-52.57, 38.67) * mm, "end": v(-52.55, 38.64) * mm});
            skArc(sketch, "E303.MirrorCS", {"start": v(-52.54, 38.14) * mm, "mid": v(-52.52, 38.16) * mm, "end": v(-52.5, 38.14) * mm});
            skLineSegment(sketch, "E304.MirrorCS", {"start": v(-57.6, 63.53) * mm, "end": v(-57.71, 63.37) * mm});
            skArc(sketch, "E305.MirrorCS", {"start": v(-52.67, 37.12) * mm, "mid": v(-52.7, 37.1) * mm, "end": v(-52.72, 37.12) * mm});
            skArc(sketch, "E306.MirrorCS", {"start": v(-53.3, 36.1) * mm, "mid": v(-53.28, 36.13) * mm, "end": v(-53.26, 36.1) * mm});
            skArc(sketch, "E307.MirrorCS", {"start": v(-52.98, 39.66) * mm, "mid": v(-52.95, 39.69) * mm, "end": v(-52.93, 39.66) * mm});
            skArc(sketch, "E308.MirrorCS", {"start": v(-52.55, 38.64) * mm, "mid": v(-52.57, 38.62) * mm, "end": v(-52.6, 38.64) * mm});
            skArc(sketch, "E309.MirrorCS", {"start": v(-52.5, 38.14) * mm, "mid": v(-52.52, 38.11) * mm, "end": v(-52.54, 38.14) * mm});
            skArc(sketch, "E310.MirrorCS", {"start": v(-52.6, 37.63) * mm, "mid": v(-52.57, 37.65) * mm, "end": v(-52.55, 37.63) * mm});
            skArc(sketch, "E311.MirrorCS", {"start": v(-58.48, 63.04) * mm, "mid": v(-58.46, 63.06) * mm, "end": v(-58.43, 63.04) * mm});
            skLineSegment(sketch, "E312.MirrorCS", {"start": v(-57.71, 63.37) * mm, "end": v(-57.85, 63.24) * mm});
            skArc(sketch, "E313.MirrorCS", {"start": v(-52.98, 36.61) * mm, "mid": v(-52.95, 36.64) * mm, "end": v(-52.93, 36.61) * mm});
            skArc(sketch, "E314.MirrorCS", {"start": v(-52.93, 36.61) * mm, "mid": v(-52.95, 36.59) * mm, "end": v(-52.98, 36.61) * mm});
            skArc(sketch, "E315.MirrorCS", {"start": v(-53.26, 36.1) * mm, "mid": v(-53.28, 36.08) * mm, "end": v(-53.3, 36.1) * mm});
            skArc(sketch, "E316.MirrorCS", {"start": v(-52.93, 39.66) * mm, "mid": v(-52.95, 39.64) * mm, "end": v(-52.98, 39.66) * mm});
            skLineSegment(sketch, "E317.MirrorCS", {"start": v(-57.47, 63.87) * mm, "end": v(-57.5, 63.72) * mm});
            skArc(sketch, "E318.MirrorCS", {"start": v(-52.55, 37.63) * mm, "mid": v(-52.57, 37.6) * mm, "end": v(-52.6, 37.63) * mm});
            skLineSegment(sketch, "E319.MirrorCS", {"start": v(-52.95, 39.66) * mm, "end": v(-52.7, 39.15) * mm});
            skLineSegment(sketch, "E320.MirrorCS", {"start": v(-52.7, 39.15) * mm, "end": v(-52.57, 38.64) * mm});
            skLineSegment(sketch, "E321.MirrorCS", {"start": v(-57.85, 63.24) * mm, "end": v(-58, 63.15) * mm});
            skLineSegment(sketch, "E322.MirrorCS", {"start": v(-52.57, 38.64) * mm, "end": v(-52.52, 38.14) * mm});
            skLineSegment(sketch, "E323.MirrorCS", {"start": v(-52.52, 38.14) * mm, "end": v(-52.57, 37.63) * mm});
            skLineSegment(sketch, "E324.MirrorCS", {"start": v(-52.57, 37.63) * mm, "end": v(-52.7, 37.12) * mm});
            skLineSegment(sketch, "E325.MirrorCS", {"start": v(-58.25, 63.06) * mm, "end": v(-58.37, 63.04) * mm});
            skLineSegment(sketch, "E326.MirrorCS", {"start": v(-52.7, 37.12) * mm, "end": v(-52.95, 36.61) * mm});
            skLineSegment(sketch, "E327.MirrorCS", {"start": v(-52.95, 36.61) * mm, "end": v(-53.28, 36.1) * mm});
            skArc(sketch, "E328.MirrorCS", {"start": v(-52.72, 39.15) * mm, "mid": v(-52.7, 39.18) * mm, "end": v(-52.67, 39.15) * mm});
            skArc(sketch, "E329.MirrorCS", {"start": v(-55.11, 35.17) * mm, "mid": v(-55.09, 35.2) * mm, "end": v(-55.06, 35.17) * mm});
            skLineSegment(sketch, "E330.MirrorCS", {"start": v(-57.46, 64.04) * mm, "end": v(-57.47, 63.87) * mm});
            skArc(sketch, "E331.MirrorCS", {"start": v(-58.43, 63.04) * mm, "mid": v(-58.46, 63.01) * mm, "end": v(-58.48, 63.04) * mm});
            skLineSegment(sketch, "E332.MirrorCS", {"start": v(-57.5, 63.72) * mm, "end": v(-57.6, 63.53) * mm});
            skLineSegment(sketch, "E333.MirrorCS", {"start": v(-58, 63.15) * mm, "end": v(-58.12, 63.1) * mm});
            skLineSegment(sketch, "E334.MirrorCS", {"start": v(-58.12, 63.1) * mm, "end": v(-58.25, 63.06) * mm});
            skLineSegment(sketch, "E335.MirrorCS", {"start": v(-58.37, 63.04) * mm, "end": v(-58.46, 63.04) * mm});
            skArc(sketch, "E336.MirrorCS", {"start": v(-55.06, 35.17) * mm, "mid": v(-55.09, 35.14) * mm, "end": v(-55.11, 35.17) * mm});
            skArc(sketch, "E337.MirrorCS", {"start": v(-53.94, 35.6) * mm, "mid": v(-53.92, 35.62) * mm, "end": v(-53.9, 35.6) * mm});
            skArc(sketch, "E338.MirrorCS", {"start": v(-54.45, 35.32) * mm, "mid": v(-54.48, 35.3) * mm, "end": v(-54.5, 35.32) * mm});
            skArc(sketch, "E339.MirrorCS", {"start": v(-55.57, 35.14) * mm, "mid": v(-55.54, 35.16) * mm, "end": v(-55.52, 35.14) * mm});
            skArc(sketch, "E340.MirrorCS", {"start": v(-53.33, 40.17) * mm, "mid": v(-53.3, 40.2) * mm, "end": v(-53.28, 40.17) * mm});
            skLineSegment(sketch, "E341.MirrorCS", {"start": v(-7.66, 12.24) * mm, "end": v(-7.66, 12.25) * mm});
            skArc(sketch, "E342.MirrorCS", {"start": v(-53.9, 35.6) * mm, "mid": v(-53.92, 35.57) * mm, "end": v(-53.94, 35.6) * mm});
            skLineSegment(sketch, "E343.MirrorCS", {"start": v(-53.92, 35.6) * mm, "end": v(-54.48, 35.32) * mm});
            skLineSegment(sketch, "E344.MirrorCS", {"start": v(-54.48, 35.32) * mm, "end": v(-55.09, 35.17) * mm});
            skLineSegment(sketch, "E345.MirrorCS", {"start": v(-55.09, 35.17) * mm, "end": v(-55.54, 35.14) * mm});
            skArc(sketch, "E346.MirrorCS", {"start": v(-55.52, 35.14) * mm, "mid": v(-55.54, 35.11) * mm, "end": v(-55.57, 35.14) * mm});
            skLineSegment(sketch, "E347.MirrorCS", {"start": v(-53.3, 40.17) * mm, "end": v(-52.95, 39.66) * mm});
            skArc(sketch, "E348.MirrorCS", {"start": v(-53.28, 40.17) * mm, "mid": v(-53.3, 40.14) * mm, "end": v(-53.33, 40.17) * mm});
            skLineSegment(sketch, "E349.MirrorCS", {"start": v(-7.66, 12.25) * mm, "end": v(-7.64, 12.39) * mm});
            skArc(sketch, "E350.MirrorCS", {"start": v(-54.5, 35.32) * mm, "mid": v(-54.48, 35.34) * mm, "end": v(-54.45, 35.32) * mm});
            skLineSegment(sketch, "E351.MirrorCS", {"start": v(-53.28, 36.1) * mm, "end": v(-53.92, 35.6) * mm});
            skLineSegment(sketch, "E352.MirrorCS", {"start": v(-7.43, 12.87) * mm, "end": v(-7.28, 13.02) * mm});
            skLineSegment(sketch, "E353.MirrorCS", {"start": v(-7.64, 12.39) * mm, "end": v(-7.63, 12.46) * mm});
            skLineSegment(sketch, "E354.MirrorCS", {"start": v(-7.28, 13.02) * mm, "end": v(-7.11, 13.13) * mm});
            skLineSegment(sketch, "E355.MirrorCS", {"start": v(-6.94, 13.2) * mm, "end": v(-6.75, 13.23) * mm});
            skLineSegment(sketch, "E356.MirrorCS", {"start": v(-7.63, 12.46) * mm, "end": v(-7.58, 12.62) * mm});
            skLineSegment(sketch, "E357.MirrorCS", {"start": v(-7.54, 12.7) * mm, "end": v(-7.43, 12.87) * mm});
            skLineSegment(sketch, "E358.MirrorCS", {"start": v(-7.56, 63.62) * mm, "end": v(-7.62, 63.78) * mm});
            skLineSegment(sketch, "E359.MirrorCS", {"start": v(-7.11, 13.13) * mm, "end": v(-6.94, 13.2) * mm});
            skLineSegment(sketch, "E360.MirrorCS", {"start": v(-6.75, 13.23) * mm, "end": v(-6.67, 13.24) * mm});
            skLineSegment(sketch, "E361.MirrorCS", {"start": v(-6.67, 13.24) * mm, "end": v(-6.66, 13.24) * mm});
            skLineSegment(sketch, "E362.MirrorCS", {"start": v(-7.12, 63.15) * mm, "end": v(-7.33, 63.3) * mm});
            skLineSegment(sketch, "E363.MirrorCS", {"start": v(-7.58, 12.62) * mm, "end": v(-7.54, 12.7) * mm});
            skArc(sketch, "E364.MirrorCS", {"start": v(-19.8, 57.98) * mm, "mid": v(-19.76, 57.95) * mm, "end": v(-19.8, 57.92) * mm});
            skLineSegment(sketch, "E365.MirrorCS", {"start": v(-7.62, 63.78) * mm, "end": v(-7.65, 63.9) * mm});
            skArc(sketch, "E366.MirrorCS", {"start": v(-34.59, 57.92) * mm, "mid": v(-34.62, 57.95) * mm, "end": v(-34.59, 57.98) * mm, "construction": true});
            skArc(sketch, "E367.MirrorCS", {"start": v(-33.38, 60.71) * mm, "mid": v(-33.41, 60.74) * mm, "end": v(-33.38, 60.77) * mm, "construction": true});
            skArc(sketch, "E368.MirrorCS", {"start": v(-54.42, 40.93) * mm, "mid": v(-54.4, 40.96) * mm, "end": v(-54.37, 40.93) * mm});
            skArc(sketch, "E369.MirrorCS", {"start": v(-19.8, 60.71) * mm, "mid": v(-19.82, 60.74) * mm, "end": v(-19.8, 60.77) * mm});
            skArc(sketch, "E370.MirrorCS", {"start": v(-53.92, 40.68) * mm, "mid": v(-53.9, 40.7) * mm, "end": v(-53.87, 40.68) * mm});
            skArc(sketch, "E371.MirrorCS", {"start": v(-18.59, 57.92) * mm, "mid": v(-18.62, 57.95) * mm, "end": v(-18.59, 57.98) * mm});
            skLineSegment(sketch, "E372.MirrorCS", {"start": v(-7.33, 63.3) * mm, "end": v(-7.48, 63.47) * mm});
            skLineSegment(sketch, "E373.MirrorCS", {"start": v(-34.59, 57.95) * mm, "end": v(-33.38, 57.95) * mm, "construction": true});
            skLineSegment(sketch, "E374.MirrorCS", {"start": v(-7.65, 63.9) * mm, "end": v(-7.66, 64.04) * mm});
            skLineSegment(sketch, "E375.MirrorCS", {"start": v(-55.47, 41.14) * mm, "end": v(-54.93, 41.08) * mm});
            skArc(sketch, "E376.MirrorCS", {"start": v(-33.38, 47) * mm, "mid": v(-33.41, 47.03) * mm, "end": v(-33.38, 47.06) * mm});
            skLineSegment(sketch, "E377.MirrorCS", {"start": v(-54.93, 41.08) * mm, "end": v(-54.4, 40.93) * mm});
            skLineSegment(sketch, "E378.MirrorCS", {"start": v(-54.4, 40.93) * mm, "end": v(-53.9, 40.68) * mm});
            skArc(sketch, "E379.MirrorCS", {"start": v(-34.59, 57.98) * mm, "mid": v(-34.56, 57.95) * mm, "end": v(-34.59, 57.92) * mm, "construction": true});
            skLineSegment(sketch, "E380.MirrorCS", {"start": v(-53.9, 40.68) * mm, "end": v(-53.3, 40.17) * mm});
            skArc(sketch, "E381.MirrorCS", {"start": v(-33.38, 57.92) * mm, "mid": v(-33.41, 57.95) * mm, "end": v(-33.38, 57.98) * mm, "construction": true});
            skArc(sketch, "E382.MirrorCS", {"start": v(-33.38, 57.98) * mm, "mid": v(-33.35, 57.95) * mm, "end": v(-33.38, 57.92) * mm, "construction": true});
            skArc(sketch, "E383.MirrorCS", {"start": v(-33.38, 60.77) * mm, "mid": v(-33.35, 60.74) * mm, "end": v(-33.38, 60.71) * mm, "construction": true});
            skArc(sketch, "E384.MirrorCS", {"start": v(-54.37, 40.93) * mm, "mid": v(-54.4, 40.9) * mm, "end": v(-54.42, 40.93) * mm});
            skArc(sketch, "E385.MirrorCS", {"start": v(-19.8, 60.77) * mm, "mid": v(-19.76, 60.74) * mm, "end": v(-19.8, 60.71) * mm});
            skArc(sketch, "E386.MirrorCS", {"start": v(-53.87, 40.68) * mm, "mid": v(-53.9, 40.65) * mm, "end": v(-53.92, 40.68) * mm});
            skLineSegment(sketch, "E387.MirrorCS", {"start": v(-18.59, 57.95) * mm, "end": v(-19.8, 57.95) * mm});
            skLineSegment(sketch, "E388.MirrorCS", {"start": v(-6.66, 63.04) * mm, "end": v(-6.9, 63.07) * mm});
            skLineSegment(sketch, "E389.MirrorCS", {"start": v(-6.9, 63.07) * mm, "end": v(-7.12, 63.15) * mm});
            skArc(sketch, "E390.MirrorCS", {"start": v(-18.59, 57.98) * mm, "mid": v(-18.55, 57.95) * mm, "end": v(-18.59, 57.92) * mm});
            skArc(sketch, "E391.MirrorCS", {"start": v(-19.8, 57.92) * mm, "mid": v(-19.82, 57.95) * mm, "end": v(-19.8, 57.98) * mm});
            skLineSegment(sketch, "E392.MirrorCS", {"start": v(-7.48, 63.47) * mm, "end": v(-7.56, 63.62) * mm});
            skArc(sketch, "E393.MirrorCS", {"start": v(-41.17, 51.47) * mm, "mid": v(-41.5, 51.15) * mm, "end": v(-41.82, 51.47) * mm});
            skArc(sketch, "E394.MirrorCS", {"start": v(-51.47, 20.36) * mm, "mid": v(-51.22, 20.6) * mm, "end": v(-50.97, 20.36) * mm});
            skArc(sketch, "E395.MirrorCS", {"start": v(-48.93, 20.36) * mm, "mid": v(-48.68, 20.6) * mm, "end": v(-48.43, 20.36) * mm});
            skArc(sketch, "E396.MirrorCS", {"start": v(-28.5, 45.73) * mm, "mid": v(-28.27, 45.5) * mm, "end": v(-28.5, 45.28) * mm});
            skArc(sketch, "E397.MirrorCS", {"start": v(-33.38, 47.06) * mm, "mid": v(-33.35, 47.03) * mm, "end": v(-33.38, 47) * mm});
            skArc(sketch, "E398.MirrorCS", {"start": v(-25.95, 45.73) * mm, "mid": v(-25.73, 45.5) * mm, "end": v(-25.95, 45.28) * mm});
            skArc(sketch, "E399.MirrorCS", {"start": v(-48.5, 14.51) * mm, "mid": v(-48.68, 14.34) * mm, "end": v(-48.86, 14.51) * mm});
            skArc(sketch, "E400.MirrorCS", {"start": v(-51.05, 14.51) * mm, "mid": v(-51.22, 14.34) * mm, "end": v(-51.4, 14.51) * mm});
            skArc(sketch, "E401.MirrorCS", {"start": v(-23.41, 45.73) * mm, "mid": v(-23.19, 45.5) * mm, "end": v(-23.41, 45.28) * mm});
            skLineSegment(sketch, "E402.MirrorCS", {"start": v(-52.5, 19.09) * mm, "end": v(-52.5, 21.63) * mm, "construction": true});
            skArc(sketch, "E403.MirrorCS", {"start": v(-41.5, 50.4) * mm, "mid": v(-42.58, 51.47) * mm, "end": v(-41.5, 52.55) * mm, "construction": true});
            skArc(sketch, "E404.MirrorCS", {"start": v(-41.5, 52.55) * mm, "mid": v(-40.42, 51.47) * mm, "end": v(-41.5, 50.4) * mm, "construction": true});
            skArc(sketch, "E405.MirrorCS", {"start": v(-50.97, 20.36) * mm, "mid": v(-51.22, 20.1) * mm, "end": v(-51.47, 20.36) * mm});
            skArc(sketch, "E406.MirrorCS", {"start": v(-10.2, 22.1) * mm, "mid": v(-10.46, 22.35) * mm, "end": v(-10.2, 22.6) * mm});
            skLineSegment(sketch, "E407.MirrorCS", {"start": v(-47.67, 15.53) * mm, "end": v(-52.24, 15.53) * mm, "construction": true});
            skArc(sketch, "E408.MirrorCS", {"start": v(-10.2, 22.6) * mm, "mid": v(-9.96, 22.35) * mm, "end": v(-10.2, 22.1) * mm});
            skArc(sketch, "E409.MirrorCS", {"start": v(-28.5, 45.28) * mm, "mid": v(-28.72, 45.5) * mm, "end": v(-28.5, 45.73) * mm});
            skLineSegment(sketch, "E410.MirrorCS", {"start": v(-52.24, 15.53) * mm, "end": v(-52.24, 13.5) * mm, "construction": true});
            skArc(sketch, "E411.MirrorCS", {"start": v(-48.43, 20.36) * mm, "mid": v(-48.68, 20.1) * mm, "end": v(-48.93, 20.36) * mm});
            skLineSegment(sketch, "E412.MirrorCS", {"start": v(-52.24, 13.5) * mm, "end": v(-47.67, 13.5) * mm, "construction": true});
            skLineSegment(sketch, "E413.MirrorCS", {"start": v(-47.67, 13.5) * mm, "end": v(-47.67, 15.53) * mm, "construction": true});
            skArc(sketch, "E414.MirrorCS", {"start": v(-25.95, 45.28) * mm, "mid": v(-26.18, 45.5) * mm, "end": v(-25.95, 45.73) * mm});
            skArc(sketch, "E415.MirrorCS", {"start": v(-48.86, 14.51) * mm, "mid": v(-48.68, 14.69) * mm, "end": v(-48.5, 14.51) * mm});
            skArc(sketch, "E416.MirrorCS", {"start": v(-51.4, 14.51) * mm, "mid": v(-51.22, 14.69) * mm, "end": v(-51.05, 14.51) * mm});
            skArc(sketch, "E417.MirrorCS", {"start": v(-46.8, 51.47) * mm, "mid": v(-46.47, 51.8) * mm, "end": v(-46.15, 51.47) * mm});
            skArc(sketch, "E418.MirrorCS", {"start": v(-46.15, 51.47) * mm, "mid": v(-46.47, 51.15) * mm, "end": v(-46.8, 51.47) * mm});
            skArc(sketch, "E419.MirrorCS", {"start": v(-23.41, 45.28) * mm, "mid": v(-23.64, 45.5) * mm, "end": v(-23.41, 45.73) * mm});
            skArc(sketch, "E420.MirrorCS", {"start": v(-46.47, 50.4) * mm, "mid": v(-47.55, 51.47) * mm, "end": v(-46.47, 52.55) * mm, "construction": true});
            skLineSegment(sketch, "E421.MirrorCS", {"start": v(-52.5, 21.63) * mm, "end": v(-47.41, 21.63) * mm, "construction": true});
            skArc(sketch, "E422.MirrorCS", {"start": v(-46.47, 52.55) * mm, "mid": v(-45.4, 51.47) * mm, "end": v(-46.47, 50.4) * mm, "construction": true});
            skLineSegment(sketch, "E423.MirrorCS", {"start": v(-47.41, 21.63) * mm, "end": v(-47.41, 19.09) * mm, "construction": true});
            skLineSegment(sketch, "E424.MirrorCS", {"start": v(-33.38, 47.03) * mm, "end": v(-34.59, 47.03) * mm, "construction": true});
            skArc(sketch, "E425.MirrorCS", {"start": v(-41.82, 51.47) * mm, "mid": v(-41.5, 51.8) * mm, "end": v(-41.17, 51.47) * mm});
            skLineSegment(sketch, "E426.MirrorCS", {"start": v(-47.41, 19.09) * mm, "end": v(-52.5, 19.09) * mm, "construction": true});
            skArc(sketch, "E427.MirrorCS", {"start": v(-10.46, 19.56) * mm, "mid": v(-10.71, 19.8) * mm, "end": v(-10.46, 20.06) * mm});
            skArc(sketch, "E428.MirrorCS", {"start": v(-13, 19.56) * mm, "mid": v(-13.25, 19.8) * mm, "end": v(-13, 20.06) * mm});
            skArc(sketch, "E429.MirrorCS", {"start": v(-13, 20.06) * mm, "mid": v(-12.75, 19.8) * mm, "end": v(-13, 19.56) * mm});
            skArc(sketch, "E430.MirrorCS", {"start": v(-10.2, 17.02) * mm, "mid": v(-10.46, 17.27) * mm, "end": v(-10.2, 17.52) * mm});
            skArc(sketch, "E431.MirrorCS", {"start": v(-12.75, 17.02) * mm, "mid": v(-13, 17.27) * mm, "end": v(-12.75, 17.52) * mm});
            skLineSegment(sketch, "E432.MirrorCS", {"start": v(-12.6, 37.63) * mm, "end": v(-12.62, 38.14) * mm});
            skArc(sketch, "E433.MirrorCS", {"start": v(-29.76, 47.82) * mm, "mid": v(-29.99, 48.04) * mm, "end": v(-29.76, 48.27) * mm});
            skLineSegment(sketch, "E434.MirrorCS", {"start": v(-12.44, 39.15) * mm, "end": v(-12.2, 39.66) * mm});
            skArc(sketch, "E435.MirrorCS", {"start": v(-12.75, 22.1) * mm, "mid": v(-13, 22.35) * mm, "end": v(-12.75, 22.6) * mm});
            skArc(sketch, "E436.MirrorCS", {"start": v(-27.22, 47.82) * mm, "mid": v(-27.45, 48.04) * mm, "end": v(-27.22, 48.27) * mm});
            skArc(sketch, "E437.MirrorCS", {"start": v(-27.22, 48.27) * mm, "mid": v(-27, 48.04) * mm, "end": v(-27.22, 47.82) * mm});
            skArc(sketch, "E438.MirrorCS", {"start": v(-13, 14.48) * mm, "mid": v(-13.25, 14.73) * mm, "end": v(-13, 14.98) * mm});
            skArc(sketch, "E439.MirrorCS", {"start": v(-10.2, 17.52) * mm, "mid": v(-9.96, 17.27) * mm, "end": v(-10.2, 17.02) * mm});
            skArc(sketch, "E440.MirrorCS", {"start": v(-12.75, 17.52) * mm, "mid": v(-12.5, 17.27) * mm, "end": v(-12.75, 17.02) * mm});
            skArc(sketch, "E441.MirrorCS", {"start": v(-10.46, 20.06) * mm, "mid": v(-10.21, 19.8) * mm, "end": v(-10.46, 19.56) * mm});
            skArc(sketch, "E442.MirrorCS", {"start": v(-54.56, 50.03) * mm, "mid": v(-55.16, 50.64) * mm, "end": v(-54.56, 51.25) * mm});
            skLineSegment(sketch, "E443.MirrorCS", {"start": v(-12.62, 38.14) * mm, "end": v(-12.6, 38.64) * mm});
            skArc(sketch, "E444.MirrorCS", {"start": v(-29.76, 48.27) * mm, "mid": v(-29.54, 48.04) * mm, "end": v(-29.76, 47.82) * mm});
            skLineSegment(sketch, "E445.MirrorCS", {"start": v(-12.6, 38.64) * mm, "end": v(-12.44, 39.15) * mm});
            skLineSegment(sketch, "E446.MirrorCS", {"start": v(-12.2, 39.66) * mm, "end": v(-11.85, 40.17) * mm});
            skLineSegment(sketch, "E447.MirrorCS", {"start": v(-11.85, 40.17) * mm, "end": v(-11.27, 40.68) * mm});
            skArc(sketch, "E448.MirrorCS", {"start": v(-12.75, 22.6) * mm, "mid": v(-12.5, 22.35) * mm, "end": v(-12.75, 22.1) * mm});
            skLineSegment(sketch, "E449.MirrorCS", {"start": v(-11.27, 40.68) * mm, "end": v(-10.81, 40.93) * mm});
            skLineSegment(sketch, "E450.MirrorCS", {"start": v(-10.81, 40.93) * mm, "end": v(-10.2, 41.1) * mm});
            skArc(sketch, "E451.MirrorCS", {"start": v(-24.68, 47.82) * mm, "mid": v(-24.9, 48.04) * mm, "end": v(-24.68, 48.27) * mm});
            skLineSegment(sketch, "E452.MirrorCS", {"start": v(-9.64, 35.14) * mm, "end": v(-10.23, 35.17) * mm});
            skArc(sketch, "E453.MirrorCS", {"start": v(-24.68, 48.27) * mm, "mid": v(-24.46, 48.04) * mm, "end": v(-24.68, 47.82) * mm});
            skLineSegment(sketch, "E454.MirrorCS", {"start": v(-10.23, 35.17) * mm, "end": v(-10.76, 35.34) * mm});
            skArc(sketch, "E455.MirrorCS", {"start": v(-54.56, 25.03) * mm, "mid": v(-55.16, 25.64) * mm, "end": v(-54.56, 26.25) * mm});
            skLineSegment(sketch, "E456.MirrorCS", {"start": v(-10.76, 35.34) * mm, "end": v(-11.24, 35.6) * mm});
            skArc(sketch, "E457.MirrorCS", {"start": v(-54.56, 26.25) * mm, "mid": v(-53.95, 25.64) * mm, "end": v(-54.56, 25.03) * mm});
            skLineSegment(sketch, "E458.MirrorCS", {"start": v(-11.24, 35.6) * mm, "end": v(-11.85, 36.1) * mm});
            skArc(sketch, "E459.MirrorCS", {"start": v(-10.56, 26.25) * mm, "mid": v(-9.95, 25.64) * mm, "end": v(-10.56, 25.03) * mm});
            skLineSegment(sketch, "E460.MirrorCS", {"start": v(-11.85, 36.1) * mm, "end": v(-12.2, 36.61) * mm});
            skArc(sketch, "E461.MirrorCS", {"start": v(-10.56, 25.03) * mm, "mid": v(-11.16, 25.64) * mm, "end": v(-10.56, 26.25) * mm});
            skLineSegment(sketch, "E462.MirrorCS", {"start": v(-12.2, 36.61) * mm, "end": v(-12.44, 37.12) * mm});
            skArc(sketch, "E463.MirrorCS", {"start": v(-54.56, 51.25) * mm, "mid": v(-53.95, 50.64) * mm, "end": v(-54.56, 50.03) * mm});
            skLineSegment(sketch, "E464.MirrorCS", {"start": v(-12.44, 37.12) * mm, "end": v(-12.6, 37.63) * mm});
            skLineSegment(sketch, "E465.MirrorCS", {"start": v(-14.15, 13.45) * mm, "end": v(-14.15, 23.59) * mm, "construction": true});
            skLineSegment(sketch, "E466.MirrorCS", {"start": v(-14.15, 23.59) * mm, "end": v(-9.07, 23.59) * mm, "construction": true});
            skLineSegment(sketch, "E467.MirrorCS", {"start": v(-9.07, 23.59) * mm, "end": v(-9.07, 13.45) * mm, "construction": true});
            skLineSegment(sketch, "E468.MirrorCS", {"start": v(-9.07, 13.45) * mm, "end": v(-14.15, 13.45) * mm, "construction": true});
            skArc(sketch, "E469.MirrorCS", {"start": v(-10.46, 14.48) * mm, "mid": v(-10.71, 14.73) * mm, "end": v(-10.46, 14.98) * mm});
            skArc(sketch, "E470.MirrorCS", {"start": v(-10.46, 14.98) * mm, "mid": v(-10.21, 14.73) * mm, "end": v(-10.46, 14.48) * mm});
            skArc(sketch, "E471.MirrorCS", {"start": v(-13, 14.98) * mm, "mid": v(-12.75, 14.73) * mm, "end": v(-13, 14.48) * mm});
            skArc(sketch, "E472.MirrorCS", {"start": v(-10.56, 51.25) * mm, "mid": v(-9.95, 50.64) * mm, "end": v(-10.56, 50.03) * mm});
            skArc(sketch, "E473.MirrorCS", {"start": v(-10.56, 50.03) * mm, "mid": v(-11.16, 50.64) * mm, "end": v(-10.56, 51.25) * mm});
            skLineSegment(sketch, "E474.MirrorCS", {"start": v(-58.46, 41.14) * mm, "end": v(-55.47, 41.14) * mm});
            skLineSegment(sketch, "E475.MirrorCS", {"start": v(-55.54, 35.14) * mm, "end": v(-58.46, 35.14) * mm});
            skLineSegment(sketch, "E476.MirrorCS", {"start": v(-6.66, 35.14) * mm, "end": v(-9.64, 35.14) * mm});
            skLineSegment(sketch, "E477.MirrorCS", {"start": v(-10.2, 41.1) * mm, "end": v(-9.64, 41.14) * mm});
            skLineSegment(sketch, "E478.MirrorCS", {"start": v(-19.8, 47.03) * mm, "end": v(-18.59, 47.03) * mm, "construction": true});
            skLineSegment(sketch, "E479.MirrorCS", {"start": v(-9.64, 41.14) * mm, "end": v(-6.66, 41.14) * mm});
            skArc(sketch, "E480.MirrorCS", {"start": v(-31.35, 52.64) * mm, "mid": v(-33.1, 54.4) * mm, "end": v(-31.35, 56.15) * mm});
            skArc(sketch, "E481.MirrorCS", {"start": v(-21.82, 56.13) * mm, "mid": v(-20.1, 54.4) * mm, "end": v(-21.82, 52.66) * mm});
            skLineSegment(sketch, "E482.MirrorCS", {"start": v(-33.38, 57.95) * mm, "end": v(-33.38, 47.03) * mm, "construction": true});
            skLineSegment(sketch, "E483.MirrorCS", {"start": v(-19.8, 60.74) * mm, "end": v(-19.8, 44.23) * mm, "construction": true});
            skLineSegment(sketch, "E484.MirrorCS", {"start": v(-34.59, 47.03) * mm, "end": v(-34.59, 57.95) * mm, "construction": true});
            skLineSegment(sketch, "E485.MirrorCS", {"start": v(-58.46, 63.04) * mm, "end": v(-58.46, 41.14) * mm});
            skLineSegment(sketch, "E486.MirrorCS", {"start": v(-7.66, 64.04) * mm, "end": v(-57.46, 64.04) * mm});
            skLineSegment(sketch, "E487.MirrorCS", {"start": v(-19.8, 44.23) * mm, "end": v(-33.38, 44.23) * mm, "construction": true});
            skLineSegment(sketch, "E488.MirrorCS", {"start": v(-58.46, 35.14) * mm, "end": v(-58.46, 13.24) * mm});
            skLineSegment(sketch, "E489.MirrorCS", {"start": v(-33.38, 44.23) * mm, "end": v(-33.38, 60.74) * mm, "construction": true});
            skLineSegment(sketch, "E490.MirrorCS", {"start": v(-33.38, 60.74) * mm, "end": v(-19.8, 60.74) * mm, "construction": true});
            skLineSegment(sketch, "E491.MirrorCS", {"start": v(-49.07, 55.47) * mm, "end": v(-49.07, 47.47) * mm, "construction": true});
            skLineSegment(sketch, "E492.MirrorCS", {"start": v(-6.66, 13.24) * mm, "end": v(-6.66, 35.14) * mm});
            skLineSegment(sketch, "E493.MirrorCS", {"start": v(-49.07, 47.47) * mm, "end": v(-38.9, 47.47) * mm, "construction": true});
            skLineSegment(sketch, "E494.MirrorCS", {"start": v(-38.9, 47.47) * mm, "end": v(-38.9, 55.47) * mm, "construction": true});
            skLineSegment(sketch, "E495.MirrorCS", {"start": v(-38.9, 55.47) * mm, "end": v(-49.07, 55.47) * mm, "construction": true});
            skLineSegment(sketch, "E496.MirrorCS", {"start": v(-19.8, 57.95) * mm, "end": v(-19.8, 47.03) * mm, "construction": true});
            skLineSegment(sketch, "E497.MirrorCS", {"start": v(-18.59, 47.03) * mm, "end": v(-18.59, 57.95) * mm, "construction": true});
            skLineSegment(sketch, "E498.MirrorCS", {"start": v(-6.66, 41.14) * mm, "end": v(-6.66, 63.04) * mm});
            skArc(sketch, "E499.MirrorCS", {"start": v(-31.35, 56.15) * mm, "mid": v(-29.6, 54.4) * mm, "end": v(-31.35, 52.64) * mm});
            skArc(sketch, "E500.MirrorCS", {"start": v(-21.82, 52.66) * mm, "mid": v(-23.56, 54.4) * mm, "end": v(-21.82, 56.13) * mm});
            skSolve(sketch);
        }
        {
            var Q0;
            Q0=makeQuery(id+"F0.imprint","IMPRINT",FACE,{"disambiguationData":[TD([[makeQuery(id+"F0.imprint","IMPRINT",EDGE,{"derivedFrom":sQuery(id+"F0.wireOp",EDGE,"E199")}),1.0]])]});
            extrude(context, id + "F1", {"entities" : qUnion([Q0]), "depth" : 1 * mm});
        }
        {
            var Q0;
            Q0=qCreatedBy(makeId("Top.planeOp"),FACE);
            var sketch = newSketch(context, id + "F2", { "sketchPlane" : qUnion([Q0])});
            skLineSegment(sketch, "E501.bottom", {"start": v(5.44, 104.39) * mm, "end": v(-70.56, 104.39) * mm});
            skLineSegment(sketch, "E501.top", {"start": v(5.44, -28.11) * mm, "end": v(-70.56, -28.11) * mm});
            skLineSegment(sketch, "E501.left", {"start": v(5.44, 104.39) * mm, "end": v(5.44, -28.11) * mm});
            skLineSegment(sketch, "E501.right", {"start": v(-70.56, 104.39) * mm, "end": v(-70.56, -28.11) * mm});
            skPoint(sketch, "E501.middle", {"position": v(-32.56, 38.14) * mm});
            skLineSegment(sketch, "E502.bottom", {"start": v(-10.56, 50.64) * mm, "end": v(-54.56, 50.64) * mm, "construction": true});
            skLineSegment(sketch, "E502.top", {"start": v(-10.56, 25.64) * mm, "end": v(-54.56, 25.64) * mm, "construction": true});
            skLineSegment(sketch, "E502.left", {"start": v(-10.56, 50.64) * mm, "end": v(-10.56, 25.64) * mm, "construction": true});
            skLineSegment(sketch, "E502.right", {"start": v(-54.56, 50.64) * mm, "end": v(-54.56, 25.64) * mm, "construction": true});
            skLineSegment(sketch, "E503.bottom", {"start": v(-56.46, 22.44) * mm, "end": v(-43.45, 22.44) * mm});
            skLineSegment(sketch, "E503.top", {"start": v(-56.46, 12.43) * mm, "end": v(-43.45, 12.43) * mm});
            skLineSegment(sketch, "E503.left", {"start": v(-56.46, 22.44) * mm, "end": v(-56.46, 12.43) * mm});
            skLineSegment(sketch, "E503.right", {"start": v(-43.45, 22.44) * mm, "end": v(-43.45, 12.43) * mm});
            skPoint(sketch, "E503.middle", {"position": v(-49.95, 17.44) * mm});
            skLineSegment(sketch, "E504.bottom", {"start": v(-50.06, 59.64) * mm, "end": v(-15.06, 59.64) * mm});
            skLineSegment(sketch, "E504.top", {"start": v(-50.06, 41.64) * mm, "end": v(-15.06, 41.64) * mm});
            skLineSegment(sketch, "E504.left", {"start": v(-50.06, 59.64) * mm, "end": v(-50.06, 41.64) * mm});
            skLineSegment(sketch, "E504.right", {"start": v(-15.06, 59.64) * mm, "end": v(-15.06, 41.64) * mm});
            skPoint(sketch, "E504.middle", {"position": v(-32.56, 50.64) * mm});
            skLineSegment(sketch, "E505.bottom", {"start": v(-62.56, -18.11) * mm, "end": v(-46.56, -18.11) * mm, "construction": true});
            skLineSegment(sketch, "E505.top", {"start": v(-62.56, -4.61) * mm, "end": v(-46.56, -4.61) * mm, "construction": true});
            skLineSegment(sketch, "E505.left", {"start": v(-62.56, -18.11) * mm, "end": v(-62.56, -4.61) * mm, "construction": true});
            skLineSegment(sketch, "E505.right", {"start": v(-46.56, -18.11) * mm, "end": v(-46.56, -4.61) * mm, "construction": true});
            skPoint(sketch, "E505.middle", {"position": v(-54.56, -11.36) * mm});
            skCircle(sketch, "E506", {"center": v(-46.56, -18.11) * mm, "radius": 2.25 * mm});
            skCircle(sketch, "E507", {"center": v(-46.56, -4.61) * mm, "radius": 2.25 * mm});
            skCircle(sketch, "E508", {"center": v(-62.56, -4.61) * mm, "radius": 2.25 * mm});
            skCircle(sketch, "E509", {"center": v(-62.56, -18.11) * mm, "radius": 2.25 * mm});
            skLineSegment(sketch, "E510", {"start": v(-32.56, 38.14) * mm, "end": v(-32.56, -28.11) * mm, "construction": true});
            skLineSegment(sketch, "E511", {"start": v(-32.56, 38.14) * mm, "end": v(5.44, 38.14) * mm, "construction": true});
            skCircle(sketch, "E512", {"center": v(-54.56, 25.64) * mm, "radius": 1 * mm});
            skCircle(sketch, "E513", {"center": v(-10.56, 25.64) * mm, "radius": 1 * mm});
            skCircle(sketch, "E514", {"center": v(-54.56, 50.64) * mm, "radius": 1 * mm});
            skCircle(sketch, "E515", {"center": v(-10.56, 50.64) * mm, "radius": 1 * mm});
            skPoint(sketch, "E516.centerSnap0", {"position": v(-46.56, -11.36) * mm});
            skLineSegment(sketch, "E517", {"start": v(-32.56, 12.24) * mm, "end": v(-32.56, 64.04) * mm, "construction": true});
            skLineSegment(sketch, "E518", {"start": v(-51.22, 20.36) * mm, "end": v(-48.68, 14.51) * mm, "construction": true});
            skLineSegment(sketch, "E519.bottom", {"start": v(-17, 12.43) * mm, "end": v(-8, 12.43) * mm});
            skLineSegment(sketch, "E519.top", {"start": v(-17, 24.35) * mm, "end": v(-8, 24.35) * mm});
            skLineSegment(sketch, "E519.left", {"start": v(-17, 12.43) * mm, "end": v(-17, 24.35) * mm});
            skLineSegment(sketch, "E519.right", {"start": v(-8, 12.43) * mm, "end": v(-8, 24.35) * mm});
            skPoint(sketch, "E520", {"position": v(-10.2, 22.35) * mm});
            skPoint(sketch, "E521", {"position": v(-13, 14.73) * mm});
            skCircle(sketch, "E522", {"center": v(-54.56, -11.36) * mm, "radius": 2.25 * mm});
            skCircle(sketch, "E523.MirrorC", {"center": v(-18.56, -4.61) * mm, "radius": 2.25 * mm});
            skCircle(sketch, "E524.MirrorC", {"center": v(-18.56, -18.11) * mm, "radius": 2.25 * mm});
            skCircle(sketch, "E525.MirrorC", {"center": v(-2.56, -4.61) * mm, "radius": 2.25 * mm});
            skCircle(sketch, "E526.MirrorC", {"center": v(-2.56, -18.11) * mm, "radius": 2.25 * mm});
            skCircle(sketch, "E527.MirrorC", {"center": v(-10.56, -11.36) * mm, "radius": 2.25 * mm});
            skCircle(sketch, "E528.MirrorC", {"center": v(-46.56, 80.89) * mm, "radius": 2.25 * mm});
            skCircle(sketch, "E529.MirrorC", {"center": v(-54.56, 87.64) * mm, "radius": 2.25 * mm});
            skCircle(sketch, "E530.MirrorC", {"center": v(-62.56, 80.89) * mm, "radius": 2.25 * mm});
            skCircle(sketch, "E531.MirrorC", {"center": v(-62.56, 94.39) * mm, "radius": 2.25 * mm});
            skCircle(sketch, "E532.MirrorC", {"center": v(-46.56, 94.39) * mm, "radius": 2.25 * mm});
            skCircle(sketch, "E533.MirrorC", {"center": v(-18.56, 94.39) * mm, "radius": 2.25 * mm});
            skCircle(sketch, "E534.MirrorC", {"center": v(-10.56, 87.64) * mm, "radius": 2.25 * mm});
            skCircle(sketch, "E535.MirrorC", {"center": v(-18.56, 80.89) * mm, "radius": 2.25 * mm});
            skCircle(sketch, "E536.MirrorC", {"center": v(-2.56, 80.89) * mm, "radius": 2.25 * mm});
            skCircle(sketch, "E537.MirrorC", {"center": v(-2.56, 94.39) * mm, "radius": 2.25 * mm});
            skSolve(sketch);
        }
        {
            var Q0;
            Q0 = qSketchRegion(id + "F2", true);
            extrude(context, id + "F3", {"entities" : qUnion([Q0]), "oppositeDirection" : true, "depth" : 10 * mm});
        }
        {
            var Q0;
            Q0=makeQuery(id+"F3.opExtrude","CAP_FACE",FACE,{"disambiguationData":[OSD([sQuery(id+"F2.wireOp",EDGE,"E501.bottom"),sQuery(id+"F2.wireOp",EDGE,"E501.top"),sQuery(id+"F2.wireOp",EDGE,"E501.left"),sQuery(id+"F2.wireOp",EDGE,"E501.right"),sQuery(id+"F2.wireOp",EDGE,"E503.bottom"),sQuery(id+"F2.wireOp",EDGE,"E503.top"),sQuery(id+"F2.wireOp",EDGE,"E503.left"),sQuery(id+"F2.wireOp",EDGE,"E503.right"),sQuery(id+"F2.wireOp",EDGE,"E504.bottom"),sQuery(id+"F2.wireOp",EDGE,"E504.top"),sQuery(id+"F2.wireOp",EDGE,"E504.left"),sQuery(id+"F2.wireOp",EDGE,"E504.right"),sQuery(id+"F2.wireOp",EDGE,"E506"),sQuery(id+"F2.wireOp",EDGE,"E507"),sQuery(id+"F2.wireOp",EDGE,"E508"),sQuery(id+"F2.wireOp",EDGE,"E509"),sQuery(id+"F2.wireOp",EDGE,"a7f934cf-8bc1-4ac3-903f-3004374b0380.MirrorC"),sQuery(id+"F2.wireOp",EDGE,"fed38925-8b72-48b8-80ed-8fcea41e4e5c.MirrorC"),sQuery(id+"F2.wireOp",EDGE,"7a01c84c-8c21-42ac-8a48-962ea41f9094.MirrorC"),sQuery(id+"F2.wireOp",EDGE,"a993f941-c50b-4866-85a1-c358772a427e.MirrorC"),sQuery(id+"F2.wireOp",EDGE,"E512"),sQuery(id+"F2.wireOp",EDGE,"E513"),sQuery(id+"F2.wireOp",EDGE,"E514"),sQuery(id+"F2.wireOp",EDGE,"E515"),sQuery(id+"F2.wireOp",EDGE,"E516"),sQuery(id+"F2.wireOp",EDGE,"8c44599b-3f82-4bdd-ad5c-46ef0bf38d90.MirrorC")])],"isStart":false});
            var sketch = newSketch(context, id + "F4", { "sketchPlane" : qUnion([Q0])});
            skCircle(sketch, "E538", {"center": v(-48.68, -20.36) * mm, "radius": 0.97 * mm});
            skCircle(sketch, "E539", {"center": v(-51.22, -20.36) * mm, "radius": 0.97 * mm});
            skCircle(sketch, "E540.1", {"center": v(-46.56, 4.61) * mm, "radius": 2.25 * mm});
            skCircle(sketch, "E540.2", {"center": v(-62.56, 4.61) * mm, "radius": 2.25 * mm});
            skCircle(sketch, "E540.3", {"center": v(-62.56, 18.11) * mm, "radius": 2.25 * mm});
            skCircle(sketch, "E540.4", {"center": v(-46.56, 18.11) * mm, "radius": 2.25 * mm});
            skCircle(sketch, "E540.11", {"center": v(-10.56, -50.64) * mm, "radius": 1 * mm});
            skCircle(sketch, "E540.12", {"center": v(-54.56, -50.64) * mm, "radius": 1 * mm});
            skCircle(sketch, "E540.13", {"center": v(-54.56, -25.64) * mm, "radius": 1 * mm, "construction": true});
            skCircle(sketch, "E540.14", {"center": v(-10.56, -25.64) * mm, "radius": 1 * mm, "construction": true});
            skPoint(sketch, "E541", {"position": v(-12.75, -22.35) * mm});
            skPoint(sketch, "E542", {"position": v(-13, -19.8) * mm});
            skPoint(sketch, "E543", {"position": v(-12.75, -17.27) * mm});
            skPoint(sketch, "E544", {"position": v(-13, -14.73) * mm});
            skPoint(sketch, "E545", {"position": v(-10.46, -14.73) * mm});
            skPoint(sketch, "E546", {"position": v(-10.2, -17.27) * mm});
            skPoint(sketch, "E547", {"position": v(-10.46, -19.8) * mm});
            skPoint(sketch, "E548", {"position": v(-10.2, -22.35) * mm});
            skCircle(sketch, "E549", {"center": v(-12.75, -22.35) * mm, "radius": 0.97 * mm});
            skCircle(sketch, "E550", {"center": v(-13, -19.8) * mm, "radius": 0.97 * mm});
            skCircle(sketch, "E551", {"center": v(-12.75, -17.27) * mm, "radius": 0.97 * mm});
            skCircle(sketch, "E552", {"center": v(-13, -14.73) * mm, "radius": 0.97 * mm});
            skCircle(sketch, "E553", {"center": v(-10.2, -17.27) * mm, "radius": 0.97 * mm});
            skCircle(sketch, "E554", {"center": v(-10.46, -19.8) * mm, "radius": 0.97 * mm});
            skCircle(sketch, "E555", {"center": v(-10.2, -22.35) * mm, "radius": 0.97 * mm});
            skCircle(sketch, "E556", {"center": v(-10.46, -14.73) * mm, "radius": 0.97 * mm});
            skLineSegment(sketch, "E557.bottom", {"start": v(-64.46, -31.64) * mm, "end": v(-0.66, -31.64) * mm});
            skLineSegment(sketch, "E557.top", {"start": v(-64.46, -7.43) * mm, "end": v(-0.66, -7.43) * mm});
            skLineSegment(sketch, "E557.left", {"start": v(-64.46, -31.64) * mm, "end": v(-64.46, -7.43) * mm});
            skLineSegment(sketch, "E557.right", {"start": v(-0.66, -31.64) * mm, "end": v(-0.66, -7.43) * mm});
            skCircle(sketch, "E558", {"center": v(-60.96, -28.14) * mm, "radius": 1.65 * mm});
            skLineSegment(sketch, "E559", {"start": v(-64.46, -19.54) * mm, "end": v(-0.66, -19.54) * mm, "construction": true});
            skLineSegment(sketch, "E560", {"start": v(-32.56, -7.43) * mm, "end": v(-32.56, -31.64) * mm, "construction": true});
            skPoint(sketch, "E561", {"position": v(-32.56, -19.54) * mm});
            skCircle(sketch, "E562", {"center": v(-60.96, -28.14) * mm, "radius": 3.5 * mm, "construction": true});
            skLineSegment(sketch, "E563", {"start": v(-32.56, 28.11) * mm, "end": v(-32.56, -7.43) * mm, "construction": true});
            skCircle(sketch, "E564.MirrorC", {"center": v(-4.16, -28.14) * mm, "radius": 1.65 * mm});
            skCircle(sketch, "E565.MirrorC", {"center": v(-60.96, -10.93) * mm, "radius": 1.65 * mm});
            skCircle(sketch, "E566.MirrorC", {"center": v(-4.16, -10.93) * mm, "radius": 1.65 * mm});
            skCircle(sketch, "E567.MirrorC", {"center": v(-4.16, -28.14) * mm, "radius": 3.5 * mm, "construction": true});
            skCircle(sketch, "E568.MirrorC", {"center": v(-60.96, -10.93) * mm, "radius": 3.5 * mm, "construction": true});
            skCircle(sketch, "E569.MirrorC", {"center": v(-4.16, -10.93) * mm, "radius": 3.5 * mm, "construction": true});
            skCircle(sketch, "E570", {"center": v(-54.56, -25.64) * mm, "radius": 1.75 * mm});
            skCircle(sketch, "E571", {"center": v(-10.56, -25.64) * mm, "radius": 1.75 * mm});
            skSolve(sketch);
        }
        {
            var Q0;
            Q0=makeQuery(id+"F4.imprint","IMPRINT",FACE,{"disambiguationData":[TD([[makeQuery(id+"F4.imprint","IMPRINT",EDGE,{"derivedFrom":sQuery(id+"F4.wireOp",EDGE,"E557.bottom")}),1.0]])]});
            var Q1;
            Q1=makeQuery(id+"F4.imprint","IMPRINT",FACE,{"disambiguationData":[TD([[makeQuery(id+"F4.imprint","IMPRINT",EDGE,{"derivedFrom":sQuery(id+"F4.wireOp",EDGE,"E538")}),-1.0]])]});
            var Q2;
            Q2=makeQuery(id+"F4.imprint","IMPRINT",FACE,{"disambiguationData":[TD([[makeQuery(id+"F4.imprint","IMPRINT",EDGE,{"derivedFrom":sQuery(id+"F4.wireOp",EDGE,"E549")}),-1.0]])]});
            extrude(context, id + "F5", {"entities" : qUnion([Q0, Q1, Q2]), "depth" : 3 * mm});
        }
        {
            var Q0;
            Q0=makeQuery(id+"F3.opExtrude","CAP_FACE",FACE,{"disambiguationData":[OSD([sQuery(id+"F2.wireOp",EDGE,"E501.bottom"),sQuery(id+"F2.wireOp",EDGE,"E501.top"),sQuery(id+"F2.wireOp",EDGE,"E501.left"),sQuery(id+"F2.wireOp",EDGE,"E501.right"),sQuery(id+"F2.wireOp",EDGE,"E503.bottom"),sQuery(id+"F2.wireOp",EDGE,"E503.top"),sQuery(id+"F2.wireOp",EDGE,"E503.left"),sQuery(id+"F2.wireOp",EDGE,"E503.right"),sQuery(id+"F2.wireOp",EDGE,"E504.bottom"),sQuery(id+"F2.wireOp",EDGE,"E504.top"),sQuery(id+"F2.wireOp",EDGE,"E504.left"),sQuery(id+"F2.wireOp",EDGE,"E504.right"),sQuery(id+"F2.wireOp",EDGE,"E506"),sQuery(id+"F2.wireOp",EDGE,"E507"),sQuery(id+"F2.wireOp",EDGE,"E508"),sQuery(id+"F2.wireOp",EDGE,"E509"),sQuery(id+"F2.wireOp",EDGE,"E512"),sQuery(id+"F2.wireOp",EDGE,"E513"),sQuery(id+"F2.wireOp",EDGE,"E514"),sQuery(id+"F2.wireOp",EDGE,"E515"),sQuery(id+"F2.wireOp",EDGE,"E519.bottom"),sQuery(id+"F2.wireOp",EDGE,"E519.top"),sQuery(id+"F2.wireOp",EDGE,"E519.left"),sQuery(id+"F2.wireOp",EDGE,"E519.right"),sQuery(id+"F2.wireOp",EDGE,"E522"),sQuery(id+"F2.wireOp",EDGE,"E523.MirrorC"),sQuery(id+"F2.wireOp",EDGE,"E524.MirrorC"),sQuery(id+"F2.wireOp",EDGE,"E525.MirrorC"),sQuery(id+"F2.wireOp",EDGE,"E526.MirrorC"),sQuery(id+"F2.wireOp",EDGE,"E527.MirrorC"),sQuery(id+"F2.wireOp",EDGE,"E528.MirrorC"),sQuery(id+"F2.wireOp",EDGE,"E529.MirrorC"),sQuery(id+"F2.wireOp",EDGE,"E530.MirrorC"),sQuery(id+"F2.wireOp",EDGE,"E531.MirrorC"),sQuery(id+"F2.wireOp",EDGE,"E532.MirrorC"),sQuery(id+"F2.wireOp",EDGE,"E533.MirrorC"),sQuery(id+"F2.wireOp",EDGE,"E534.MirrorC"),sQuery(id+"F2.wireOp",EDGE,"E535.MirrorC"),sQuery(id+"F2.wireOp",EDGE,"E536.MirrorC"),sQuery(id+"F2.wireOp",EDGE,"E537.MirrorC")])],"isStart":false});
            var sketch = newSketch(context, id + "F6", { "sketchPlane" : qUnion([Q0])});
            skCircle(sketch, "E572.0", {"center": v(-60.96, -10.93) * mm, "radius": 1.65 * mm});
            skCircle(sketch, "E572.1", {"center": v(-60.96, -28.14) * mm, "radius": 1.65 * mm});
            skCircle(sketch, "E572.2", {"center": v(-4.16, -10.93) * mm, "radius": 1.65 * mm});
            skCircle(sketch, "E572.3", {"center": v(-4.16, -28.14) * mm, "radius": 1.65 * mm});
            skSolve(sketch);
        }
        {
            var Q0;
            Q0 = qSketchRegion(id + "F6", true);
            extrude(context, id + "F7", {"entities" : qUnion([Q0]), "operationType" : NewBodyOperationType.REMOVE, "endBound" : BoundingType.UP_TO_NEXT, "oppositeDirection" : true, "depth" : 25 * mm});
        }
        {
            var Q0;
            Q0=makeQuery(id+"F3.opExtrude","CAP_FACE",FACE,{"disambiguationData":[OSD([sQuery(id+"F2.wireOp",EDGE,"E501.bottom"),sQuery(id+"F2.wireOp",EDGE,"E501.top"),sQuery(id+"F2.wireOp",EDGE,"E501.left"),sQuery(id+"F2.wireOp",EDGE,"E501.right"),sQuery(id+"F2.wireOp",EDGE,"E503.bottom"),sQuery(id+"F2.wireOp",EDGE,"E503.top"),sQuery(id+"F2.wireOp",EDGE,"E503.left"),sQuery(id+"F2.wireOp",EDGE,"E503.right"),sQuery(id+"F2.wireOp",EDGE,"E504.bottom"),sQuery(id+"F2.wireOp",EDGE,"E504.top"),sQuery(id+"F2.wireOp",EDGE,"E504.left"),sQuery(id+"F2.wireOp",EDGE,"E504.right"),sQuery(id+"F2.wireOp",EDGE,"E506"),sQuery(id+"F2.wireOp",EDGE,"E507"),sQuery(id+"F2.wireOp",EDGE,"E508"),sQuery(id+"F2.wireOp",EDGE,"E509"),sQuery(id+"F2.wireOp",EDGE,"E512"),sQuery(id+"F2.wireOp",EDGE,"E513"),sQuery(id+"F2.wireOp",EDGE,"E514"),sQuery(id+"F2.wireOp",EDGE,"E515"),sQuery(id+"F2.wireOp",EDGE,"E519.bottom"),sQuery(id+"F2.wireOp",EDGE,"E519.top"),sQuery(id+"F2.wireOp",EDGE,"E519.left"),sQuery(id+"F2.wireOp",EDGE,"E519.right"),sQuery(id+"F2.wireOp",EDGE,"E522"),sQuery(id+"F2.wireOp",EDGE,"E523.MirrorC"),sQuery(id+"F2.wireOp",EDGE,"E524.MirrorC"),sQuery(id+"F2.wireOp",EDGE,"E525.MirrorC"),sQuery(id+"F2.wireOp",EDGE,"E526.MirrorC"),sQuery(id+"F2.wireOp",EDGE,"E527.MirrorC"),sQuery(id+"F2.wireOp",EDGE,"E528.MirrorC"),sQuery(id+"F2.wireOp",EDGE,"E529.MirrorC"),sQuery(id+"F2.wireOp",EDGE,"E530.MirrorC"),sQuery(id+"F2.wireOp",EDGE,"E531.MirrorC"),sQuery(id+"F2.wireOp",EDGE,"E532.MirrorC"),sQuery(id+"F2.wireOp",EDGE,"E533.MirrorC"),sQuery(id+"F2.wireOp",EDGE,"E534.MirrorC"),sQuery(id+"F2.wireOp",EDGE,"E535.MirrorC"),sQuery(id+"F2.wireOp",EDGE,"E536.MirrorC"),sQuery(id+"F2.wireOp",EDGE,"E537.MirrorC")])],"isStart":true});
            var sketch = newSketch(context, id + "F8", { "sketchPlane" : qUnion([Q0])});
            skPoint(sketch, "E573", {"position": v(-60.96, 10.93) * mm});
            skCircle(sketch, "E574.cCircle", {"center": v(-60.96, 10.93) * mm, "radius": 2.83 * mm, "construction": true});
            skLineSegment(sketch, "E574.0", {"start": v(-59.32, 8.1) * mm, "end": v(-62.59, 8.1) * mm});
            skLineSegment(sketch, "E574.1", {"start": v(-62.59, 8.1) * mm, "end": v(-64.22, 10.93) * mm});
            skLineSegment(sketch, "E574.2", {"start": v(-64.22, 10.93) * mm, "end": v(-62.59, 13.76) * mm});
            skLineSegment(sketch, "E574.3", {"start": v(-62.59, 13.76) * mm, "end": v(-59.32, 13.76) * mm});
            skLineSegment(sketch, "E574.4", {"start": v(-59.32, 13.76) * mm, "end": v(-57.7, 10.93) * mm});
            skLineSegment(sketch, "E574.5", {"start": v(-57.7, 10.93) * mm, "end": v(-59.32, 8.1) * mm});
            skPoint(sketch, "E574.0.midPoint", {"position": v(-60.96, 8.1) * mm});
            skCircle(sketch, "E575.cCircle", {"center": v(-60.96, 28.14) * mm, "radius": 2.83 * mm, "construction": true});
            skLineSegment(sketch, "E575.0", {"start": v(-59.32, 25.31) * mm, "end": v(-62.59, 25.31) * mm});
            skLineSegment(sketch, "E575.1", {"start": v(-62.59, 25.31) * mm, "end": v(-64.22, 28.14) * mm});
            skLineSegment(sketch, "E575.2", {"start": v(-64.22, 28.14) * mm, "end": v(-62.59, 30.96) * mm});
            skLineSegment(sketch, "E575.3", {"start": v(-62.59, 30.96) * mm, "end": v(-59.32, 30.96) * mm});
            skLineSegment(sketch, "E575.4", {"start": v(-59.32, 30.96) * mm, "end": v(-57.7, 28.14) * mm});
            skLineSegment(sketch, "E575.5", {"start": v(-57.7, 28.14) * mm, "end": v(-59.32, 25.31) * mm});
            skPoint(sketch, "E575.0.midPoint", {"position": v(-60.96, 25.31) * mm});
            skCircle(sketch, "E576.cCircle", {"center": v(-4.16, 28.14) * mm, "radius": 2.83 * mm, "construction": true});
            skLineSegment(sketch, "E576.0", {"start": v(-2.52, 25.31) * mm, "end": v(-5.79, 25.31) * mm});
            skLineSegment(sketch, "E576.1", {"start": v(-5.79, 25.31) * mm, "end": v(-7.42, 28.14) * mm});
            skLineSegment(sketch, "E576.2", {"start": v(-7.42, 28.14) * mm, "end": v(-5.79, 30.96) * mm});
            skLineSegment(sketch, "E576.3", {"start": v(-5.79, 30.96) * mm, "end": v(-2.52, 30.96) * mm});
            skLineSegment(sketch, "E576.4", {"start": v(-2.52, 30.96) * mm, "end": v(-0.9, 28.14) * mm});
            skLineSegment(sketch, "E576.5", {"start": v(-0.9, 28.14) * mm, "end": v(-2.52, 25.31) * mm});
            skPoint(sketch, "E576.0.midPoint", {"position": v(-4.16, 25.31) * mm});
            skCircle(sketch, "E577.cCircle", {"center": v(-4.16, 10.93) * mm, "radius": 2.83 * mm, "construction": true});
            skLineSegment(sketch, "E577.0", {"start": v(-5.79, 13.76) * mm, "end": v(-2.52, 13.76) * mm});
            skLineSegment(sketch, "E577.1", {"start": v(-2.52, 13.76) * mm, "end": v(-0.9, 10.93) * mm});
            skLineSegment(sketch, "E577.2", {"start": v(-0.9, 10.93) * mm, "end": v(-2.52, 8.1) * mm});
            skLineSegment(sketch, "E577.3", {"start": v(-2.52, 8.1) * mm, "end": v(-5.79, 8.1) * mm});
            skLineSegment(sketch, "E577.4", {"start": v(-5.79, 8.1) * mm, "end": v(-7.42, 10.93) * mm});
            skLineSegment(sketch, "E577.5", {"start": v(-7.42, 10.93) * mm, "end": v(-5.79, 13.76) * mm});
            skPoint(sketch, "E577.0.midPoint", {"position": v(-4.16, 13.76) * mm});
            skSolve(sketch);
        }
        {
            var Q0;
            Q0=makeQuery(id+"F8.imprint","IMPRINT",FACE,{"disambiguationData":[TD([[makeQuery(id+"F8.imprint","IMPRINT",EDGE,{"derivedFrom":sQuery(id+"F8.wireOp",EDGE,"E575.0")}),-1.0]])]});
            var Q1;
            Q1=makeQuery(id+"F8.imprint","IMPRINT",FACE,{"disambiguationData":[TD([[makeQuery(id+"F8.imprint","IMPRINT",EDGE,{"derivedFrom":sQuery(id+"F8.wireOp",EDGE,"E574.0")}),-1.0]])]});
            var Q2;
            Q2=makeQuery(id+"F8.imprint","IMPRINT",FACE,{"disambiguationData":[TD([[makeQuery(id+"F8.imprint","IMPRINT",EDGE,{"derivedFrom":sQuery(id+"F8.wireOp",EDGE,"E576.0")}),-1.0]])]});
            var Q3;
            Q3=makeQuery(id+"F8.imprint","IMPRINT",FACE,{"disambiguationData":[TD([[makeQuery(id+"F8.imprint","IMPRINT",EDGE,{"derivedFrom":sQuery(id+"F8.wireOp",EDGE,"E577.0")}),-1.0]])]});
            extrude(context, id + "F9", {"entities" : qUnion([Q0, Q1, Q2, Q3]), "operationType" : NewBodyOperationType.REMOVE, "oppositeDirection" : true, "depth" : 7 * mm});
        }
        {
            var Q0;
            Q0=makeQuery(id+"F3.opExtrude","CAP_FACE",FACE,{"disambiguationData":[OSD([sQuery(id+"F2.wireOp",EDGE,"E501.bottom"),sQuery(id+"F2.wireOp",EDGE,"E501.top"),sQuery(id+"F2.wireOp",EDGE,"E501.left"),sQuery(id+"F2.wireOp",EDGE,"E501.right"),sQuery(id+"F2.wireOp",EDGE,"E503.bottom"),sQuery(id+"F2.wireOp",EDGE,"E503.top"),sQuery(id+"F2.wireOp",EDGE,"E503.left"),sQuery(id+"F2.wireOp",EDGE,"E503.right"),sQuery(id+"F2.wireOp",EDGE,"E504.bottom"),sQuery(id+"F2.wireOp",EDGE,"E504.top"),sQuery(id+"F2.wireOp",EDGE,"E504.left"),sQuery(id+"F2.wireOp",EDGE,"E504.right"),sQuery(id+"F2.wireOp",EDGE,"E506"),sQuery(id+"F2.wireOp",EDGE,"E507"),sQuery(id+"F2.wireOp",EDGE,"E508"),sQuery(id+"F2.wireOp",EDGE,"E509"),sQuery(id+"F2.wireOp",EDGE,"E512"),sQuery(id+"F2.wireOp",EDGE,"E513"),sQuery(id+"F2.wireOp",EDGE,"E514"),sQuery(id+"F2.wireOp",EDGE,"E515"),sQuery(id+"F2.wireOp",EDGE,"E519.bottom"),sQuery(id+"F2.wireOp",EDGE,"E519.top"),sQuery(id+"F2.wireOp",EDGE,"E519.left"),sQuery(id+"F2.wireOp",EDGE,"E519.right"),sQuery(id+"F2.wireOp",EDGE,"E522"),sQuery(id+"F2.wireOp",EDGE,"E523.MirrorC"),sQuery(id+"F2.wireOp",EDGE,"E524.MirrorC"),sQuery(id+"F2.wireOp",EDGE,"E525.MirrorC"),sQuery(id+"F2.wireOp",EDGE,"E526.MirrorC"),sQuery(id+"F2.wireOp",EDGE,"E527.MirrorC"),sQuery(id+"F2.wireOp",EDGE,"E528.MirrorC"),sQuery(id+"F2.wireOp",EDGE,"E529.MirrorC"),sQuery(id+"F2.wireOp",EDGE,"E530.MirrorC"),sQuery(id+"F2.wireOp",EDGE,"E531.MirrorC"),sQuery(id+"F2.wireOp",EDGE,"E532.MirrorC"),sQuery(id+"F2.wireOp",EDGE,"E533.MirrorC"),sQuery(id+"F2.wireOp",EDGE,"E534.MirrorC"),sQuery(id+"F2.wireOp",EDGE,"E535.MirrorC"),sQuery(id+"F2.wireOp",EDGE,"E536.MirrorC"),sQuery(id+"F2.wireOp",EDGE,"E537.MirrorC")])],"isStart":false});
            var sketch = newSketch(context, id + "F10", { "sketchPlane" : qUnion([Q0])});
            skLineSegment(sketch, "E578.0", {"start": v(-65.96, -5.93) * mm, "end": v(-65.96, -33.14) * mm});
            skLineSegment(sketch, "E578.1", {"start": v(0.84, -5.93) * mm, "end": v(-65.96, -5.93) * mm});
            skLineSegment(sketch, "E578.2", {"start": v(0.84, -33.14) * mm, "end": v(0.84, -5.93) * mm});
            skLineSegment(sketch, "E578.3", {"start": v(-65.96, -33.14) * mm, "end": v(0.84, -33.14) * mm});
            skSolve(sketch);
        }
        {
            var Q0;
            Q0=makeQuery(id+"F10.imprint","IMPRINT",FACE,{"disambiguationData":[TD([[makeQuery(id+"F10.imprint","IMPRINT",EDGE,{"derivedFrom":sQuery(id+"F10.wireOp",EDGE,"E578.0")}),-1.0]])]});
            extrude(context, id + "F11", {"entities" : qUnion([Q0]), "operationType" : NewBodyOperationType.ADD, "depth" : 7 * mm});
        }
        {
            var Q0;
            {var subQ0=sQuery(id+"F2.wireOp",EDGE,"E501.right");var subQ1=sQuery(id+"F2.wireOp",EDGE,"E501.top");Q0=makeQuery(id+"Fdj7GERhAkfk1yc_2.boolean.opBoolean","MERGE",EDGE,{"derivedFrom":[makeQuery(id+"F3.opExtrude","SWEPT_EDGE",EDGE,{"disambiguationData":[OSD([subQ1,subQ0])]}),makeQuery(id+"Fdj7GERhAkfk1yc_2.opExtrude","SWEPT_EDGE",EDGE,{"disambiguationData":[OSD([subQ1,subQ0])]})]});}
            var Q1;
            {var subQ0=sQuery(id+"F2.wireOp",EDGE,"E501.left");var subQ1=sQuery(id+"F2.wireOp",EDGE,"E501.top");Q1=makeQuery(id+"Fdj7GERhAkfk1yc_2.boolean.opBoolean","MERGE",EDGE,{"derivedFrom":[makeQuery(id+"F3.opExtrude","SWEPT_EDGE",EDGE,{"disambiguationData":[OSD([subQ1,subQ0])]}),makeQuery(id+"Fdj7GERhAkfk1yc_2.opExtrude","SWEPT_EDGE",EDGE,{"disambiguationData":[OSD([subQ1,subQ0])]})]});}
            var Q2;
            {var subQ0=sQuery(id+"F2.wireOp",EDGE,"E501.left");var subQ1=sQuery(id+"F2.wireOp",EDGE,"E501.bottom");Q2=makeQuery(id+"Fdj7GERhAkfk1yc_2.boolean.opBoolean","MERGE",EDGE,{"derivedFrom":[makeQuery(id+"F3.opExtrude","SWEPT_EDGE",EDGE,{"disambiguationData":[OSD([subQ1,subQ0])]}),makeQuery(id+"Fdj7GERhAkfk1yc_2.opExtrude","SWEPT_EDGE",EDGE,{"disambiguationData":[OSD([subQ1,subQ0])]})]});}
            var Q3;
            {var subQ0=sQuery(id+"F2.wireOp",EDGE,"E501.right");var subQ1=sQuery(id+"F2.wireOp",EDGE,"E501.bottom");Q3=makeQuery(id+"Fdj7GERhAkfk1yc_2.boolean.opBoolean","MERGE",EDGE,{"derivedFrom":[makeQuery(id+"F3.opExtrude","SWEPT_EDGE",EDGE,{"disambiguationData":[OSD([subQ1,subQ0])]}),makeQuery(id+"Fdj7GERhAkfk1yc_2.opExtrude","SWEPT_EDGE",EDGE,{"disambiguationData":[OSD([subQ1,subQ0])]})]});}
            fillet(context, id + "F12", {"entities" : qUnion([Q0, Q1, Q2, Q3]), "radius" : 10 * mm, "tangentPropagation" : true, "allowEdgeOverflow" : false});
        }
        {
            var Q0;
            Q0=makeQuery(id+"F3.opExtrude","CAP_FACE",FACE,{"disambiguationData":[OSD([sQuery(id+"F2.wireOp",EDGE,"E501.bottom"),sQuery(id+"F2.wireOp",EDGE,"E501.top"),sQuery(id+"F2.wireOp",EDGE,"E501.left"),sQuery(id+"F2.wireOp",EDGE,"E501.right"),sQuery(id+"F2.wireOp",EDGE,"E503.bottom"),sQuery(id+"F2.wireOp",EDGE,"E503.top"),sQuery(id+"F2.wireOp",EDGE,"E503.left"),sQuery(id+"F2.wireOp",EDGE,"E503.right"),sQuery(id+"F2.wireOp",EDGE,"E504.bottom"),sQuery(id+"F2.wireOp",EDGE,"E504.top"),sQuery(id+"F2.wireOp",EDGE,"E504.left"),sQuery(id+"F2.wireOp",EDGE,"E504.right"),sQuery(id+"F2.wireOp",EDGE,"E506"),sQuery(id+"F2.wireOp",EDGE,"E507"),sQuery(id+"F2.wireOp",EDGE,"E508"),sQuery(id+"F2.wireOp",EDGE,"E509"),sQuery(id+"F2.wireOp",EDGE,"E512"),sQuery(id+"F2.wireOp",EDGE,"E513"),sQuery(id+"F2.wireOp",EDGE,"E514"),sQuery(id+"F2.wireOp",EDGE,"E515"),sQuery(id+"F2.wireOp",EDGE,"E519.bottom"),sQuery(id+"F2.wireOp",EDGE,"E519.top"),sQuery(id+"F2.wireOp",EDGE,"E519.left"),sQuery(id+"F2.wireOp",EDGE,"E519.right"),sQuery(id+"F2.wireOp",EDGE,"E522"),sQuery(id+"F2.wireOp",EDGE,"E523.MirrorC"),sQuery(id+"F2.wireOp",EDGE,"E524.MirrorC"),sQuery(id+"F2.wireOp",EDGE,"E525.MirrorC"),sQuery(id+"F2.wireOp",EDGE,"E526.MirrorC"),sQuery(id+"F2.wireOp",EDGE,"E527.MirrorC"),sQuery(id+"F2.wireOp",EDGE,"E528.MirrorC"),sQuery(id+"F2.wireOp",EDGE,"E529.MirrorC"),sQuery(id+"F2.wireOp",EDGE,"E530.MirrorC"),sQuery(id+"F2.wireOp",EDGE,"E531.MirrorC"),sQuery(id+"F2.wireOp",EDGE,"E532.MirrorC"),sQuery(id+"F2.wireOp",EDGE,"E533.MirrorC"),sQuery(id+"F2.wireOp",EDGE,"E534.MirrorC"),sQuery(id+"F2.wireOp",EDGE,"E535.MirrorC"),sQuery(id+"F2.wireOp",EDGE,"E536.MirrorC"),sQuery(id+"F2.wireOp",EDGE,"E537.MirrorC")])],"isStart":true});
            var sketch = newSketch(context, id + "F13", { "sketchPlane" : qUnion([Q0])});
            skCircle(sketch, "E579", {"center": v(-54.56, 87.64) * mm, "radius": 3.6 * mm});
            skCircle(sketch, "E580", {"center": v(-10.56, 87.64) * mm, "radius": 3.6 * mm});
            skCircle(sketch, "E581", {"center": v(-10.56, -11.36) * mm, "radius": 3.6 * mm});
            skCircle(sketch, "E582", {"center": v(-54.56, -11.36) * mm, "radius": 3.6 * mm});
            skSolve(sketch);
        }
        {
            var Q0;
            Q0 = qSketchRegion(id + "F13", true);
            extrude(context, id + "F14", {"entities" : qUnion([Q0]), "operationType" : NewBodyOperationType.REMOVE, "oppositeDirection" : true, "depth" : 5 * mm});
        }
        {
            var Q0;
            Q0=makeQuery(id+"F11.opExtrude","CAP_FACE",FACE,{"disambiguationData":[OSD([sQuery(id+"F2.wireOp",EDGE,"E501.bottom"),sQuery(id+"F2.wireOp",EDGE,"E501.top"),sQuery(id+"F2.wireOp",EDGE,"E501.left"),sQuery(id+"F2.wireOp",EDGE,"E501.right"),sQuery(id+"F2.wireOp",EDGE,"E504.bottom"),sQuery(id+"F2.wireOp",EDGE,"E504.top"),sQuery(id+"F2.wireOp",EDGE,"E504.left"),sQuery(id+"F2.wireOp",EDGE,"E504.right"),sQuery(id+"F2.wireOp",EDGE,"E506"),sQuery(id+"F2.wireOp",EDGE,"E507"),sQuery(id+"F2.wireOp",EDGE,"E508"),sQuery(id+"F2.wireOp",EDGE,"E509"),sQuery(id+"F2.wireOp",EDGE,"E514"),sQuery(id+"F2.wireOp",EDGE,"E515"),sQuery(id+"F2.wireOp",EDGE,"E522"),sQuery(id+"F2.wireOp",EDGE,"E523.MirrorC"),sQuery(id+"F2.wireOp",EDGE,"E524.MirrorC"),sQuery(id+"F2.wireOp",EDGE,"E525.MirrorC"),sQuery(id+"F2.wireOp",EDGE,"E526.MirrorC"),sQuery(id+"F2.wireOp",EDGE,"E527.MirrorC"),sQuery(id+"F2.wireOp",EDGE,"E528.MirrorC"),sQuery(id+"F2.wireOp",EDGE,"E529.MirrorC"),sQuery(id+"F2.wireOp",EDGE,"E530.MirrorC"),sQuery(id+"F2.wireOp",EDGE,"E531.MirrorC"),sQuery(id+"F2.wireOp",EDGE,"E532.MirrorC"),sQuery(id+"F2.wireOp",EDGE,"E533.MirrorC"),sQuery(id+"F2.wireOp",EDGE,"E534.MirrorC"),sQuery(id+"F2.wireOp",EDGE,"E535.MirrorC"),sQuery(id+"F2.wireOp",EDGE,"E536.MirrorC"),sQuery(id+"F2.wireOp",EDGE,"E537.MirrorC"),sQuery(id+"F10.wireOp",EDGE,"E578.0"),sQuery(id+"F10.wireOp",EDGE,"E578.1"),sQuery(id+"F10.wireOp",EDGE,"E578.2"),sQuery(id+"F10.wireOp",EDGE,"E578.3")])],"isStart":false});
            var sketch = newSketch(context, id + "F15", { "sketchPlane" : qUnion([Q0])});
            skCircle(sketch, "E583.cCircle", {"center": v(-18.56, 18.11) * mm, "radius": 3.55 * mm, "construction": true});
            skLineSegment(sketch, "E583.0", {"start": v(-20.6, 21.66) * mm, "end": v(-16.5, 21.66) * mm});
            skLineSegment(sketch, "E583.1", {"start": v(-16.5, 21.66) * mm, "end": v(-14.46, 18.11) * mm});
            skLineSegment(sketch, "E583.2", {"start": v(-14.46, 18.11) * mm, "end": v(-16.5, 14.56) * mm});
            skLineSegment(sketch, "E583.3", {"start": v(-16.5, 14.56) * mm, "end": v(-20.6, 14.56) * mm});
            skLineSegment(sketch, "E583.4", {"start": v(-20.6, 14.56) * mm, "end": v(-22.65, 18.11) * mm});
            skLineSegment(sketch, "E583.5", {"start": v(-22.65, 18.11) * mm, "end": v(-20.6, 21.66) * mm});
            skPoint(sketch, "E583.0.midPoint", {"position": v(-18.56, 21.66) * mm});
            skLineSegment(sketch, "E584", {"start": v(-10.56, 11.36) * mm, "end": v(-10.56, 28.11) * mm, "construction": true});
            skLineSegment(sketch, "E585", {"start": v(-10.56, 11.36) * mm, "end": v(5.44, 11.36) * mm, "construction": true});
            skLineSegment(sketch, "E586.MirrorCS", {"start": v(-4.6, 21.66) * mm, "end": v(-6.65, 18.11) * mm});
            skLineSegment(sketch, "E587.MirrorCS", {"start": v(-0.5, 21.66) * mm, "end": v(-4.6, 21.66) * mm});
            skLineSegment(sketch, "E588.MirrorCS", {"start": v(1.54, 18.11) * mm, "end": v(-0.5, 21.66) * mm});
            skLineSegment(sketch, "E589.MirrorCS", {"start": v(-0.5, 14.56) * mm, "end": v(1.54, 18.11) * mm});
            skLineSegment(sketch, "E590.MirrorCS", {"start": v(-4.6, 14.56) * mm, "end": v(-0.5, 14.56) * mm});
            skLineSegment(sketch, "E591.MirrorCS", {"start": v(-6.65, 18.11) * mm, "end": v(-4.6, 14.56) * mm});
            skLineSegment(sketch, "E592.MirrorCS", {"start": v(-14.46, 4.61) * mm, "end": v(-16.5, 8.16) * mm});
            skLineSegment(sketch, "E593.MirrorCS", {"start": v(-16.5, 1.06) * mm, "end": v(-14.46, 4.61) * mm});
            skLineSegment(sketch, "E594.MirrorCS", {"start": v(-20.6, 1.06) * mm, "end": v(-16.5, 1.06) * mm});
            skLineSegment(sketch, "E595.MirrorCS", {"start": v(-22.65, 4.61) * mm, "end": v(-20.6, 1.06) * mm});
            skLineSegment(sketch, "E596.MirrorCS", {"start": v(-20.6, 8.16) * mm, "end": v(-22.65, 4.61) * mm});
            skLineSegment(sketch, "E597.MirrorCS", {"start": v(-16.5, 8.16) * mm, "end": v(-20.6, 8.16) * mm});
            skLineSegment(sketch, "E598.MirrorCS", {"start": v(-6.65, 4.61) * mm, "end": v(-4.6, 8.16) * mm});
            skLineSegment(sketch, "E599.MirrorCS", {"start": v(-4.6, 1.06) * mm, "end": v(-6.65, 4.61) * mm});
            skLineSegment(sketch, "E600.MirrorCS", {"start": v(-0.5, 1.06) * mm, "end": v(-4.6, 1.06) * mm});
            skLineSegment(sketch, "E601.MirrorCS", {"start": v(1.54, 4.61) * mm, "end": v(-0.5, 1.06) * mm});
            skLineSegment(sketch, "E602.MirrorCS", {"start": v(-0.5, 8.16) * mm, "end": v(1.54, 4.61) * mm});
            skLineSegment(sketch, "E603.MirrorCS", {"start": v(-4.6, 8.16) * mm, "end": v(-0.5, 8.16) * mm});
            skSolve(sketch);
        }
        {
            var Q0;
            Q0 = qSketchRegion(id + "F15", true);
            extrude(context, id + "F16", {"entities" : qUnion([Q0]), "operationType" : NewBodyOperationType.REMOVE, "oppositeDirection" : true, "depth" : 12 * mm});
        }
        {
            var Q0;
            {var subQ0=sQuery(id+"F2.wireOp",EDGE,"E501.left");Q0=makeQuery(id+"F11.boolean.opBoolean","MERGE",FACE,{"derivedFrom":[makeQuery(id+"F3.opExtrude","SWEPT_FACE",FACE,{"disambiguationData":[OSD([subQ0])]}),makeQuery(id+"F11.opExtrude","SWEPT_FACE",FACE,{"disambiguationData":[OSD([subQ0])]})]});}
            var Q1;
            {var subQ0=sQuery(id+"F2.wireOp",EDGE,"E501.right");Q1=makeQuery(id+"F11.boolean.opBoolean","MERGE",FACE,{"derivedFrom":[makeQuery(id+"F3.opExtrude","SWEPT_FACE",FACE,{"disambiguationData":[OSD([subQ0])]}),makeQuery(id+"F11.opExtrude","SWEPT_FACE",FACE,{"disambiguationData":[OSD([subQ0])]})]});}
            cPlane(context, id + "F17", {"entities" : qUnion([Q0, Q1]), "cplaneType" : CPlaneType.MID_PLANE, "offset" : 25 * mm, "width" : 150 * mm, "height" : 150 * mm});
        }
        {
            var Q0;
            {var subQ0=sQuery(id+"F2.wireOp",EDGE,"E501.top");Q0=makeQuery(id+"F11.boolean.opBoolean","MERGE",FACE,{"derivedFrom":[makeQuery(id+"F3.opExtrude","SWEPT_FACE",FACE,{"disambiguationData":[OSD([subQ0])]}),makeQuery(id+"F11.opExtrude","SWEPT_FACE",FACE,{"disambiguationData":[OSD([subQ0])]})]});}
            var Q1;
            {var subQ0=sQuery(id+"F2.wireOp",EDGE,"E501.bottom");Q1=makeQuery(id+"F11.boolean.opBoolean","MERGE",FACE,{"derivedFrom":[makeQuery(id+"F3.opExtrude","SWEPT_FACE",FACE,{"disambiguationData":[OSD([subQ0])]}),makeQuery(id+"F11.opExtrude","SWEPT_FACE",FACE,{"disambiguationData":[OSD([subQ0])]})]});}
            cPlane(context, id + "F18", {"entities" : qUnion([Q0, Q1]), "cplaneType" : CPlaneType.MID_PLANE, "offset" : 25 * mm, "width" : 150 * mm, "height" : 150 * mm});
        }
        {
            var Q0;
            Q0=makeQuery(id+"F11.opExtrude","CAP_FACE",FACE,{"disambiguationData":[OSD([sQuery(id+"F2.wireOp",EDGE,"E501.bottom"),sQuery(id+"F2.wireOp",EDGE,"E501.top"),sQuery(id+"F2.wireOp",EDGE,"E501.left"),sQuery(id+"F2.wireOp",EDGE,"E501.right"),sQuery(id+"F2.wireOp",EDGE,"E504.bottom"),sQuery(id+"F2.wireOp",EDGE,"E504.top"),sQuery(id+"F2.wireOp",EDGE,"E504.left"),sQuery(id+"F2.wireOp",EDGE,"E504.right"),sQuery(id+"F2.wireOp",EDGE,"E506"),sQuery(id+"F2.wireOp",EDGE,"E507"),sQuery(id+"F2.wireOp",EDGE,"E508"),sQuery(id+"F2.wireOp",EDGE,"E509"),sQuery(id+"F2.wireOp",EDGE,"E514"),sQuery(id+"F2.wireOp",EDGE,"E515"),sQuery(id+"F2.wireOp",EDGE,"E522"),sQuery(id+"F2.wireOp",EDGE,"E523.MirrorC"),sQuery(id+"F2.wireOp",EDGE,"E524.MirrorC"),sQuery(id+"F2.wireOp",EDGE,"E525.MirrorC"),sQuery(id+"F2.wireOp",EDGE,"E526.MirrorC"),sQuery(id+"F2.wireOp",EDGE,"E527.MirrorC"),sQuery(id+"F2.wireOp",EDGE,"E528.MirrorC"),sQuery(id+"F2.wireOp",EDGE,"E529.MirrorC"),sQuery(id+"F2.wireOp",EDGE,"E530.MirrorC"),sQuery(id+"F2.wireOp",EDGE,"E531.MirrorC"),sQuery(id+"F2.wireOp",EDGE,"E532.MirrorC"),sQuery(id+"F2.wireOp",EDGE,"E533.MirrorC"),sQuery(id+"F2.wireOp",EDGE,"E534.MirrorC"),sQuery(id+"F2.wireOp",EDGE,"E535.MirrorC"),sQuery(id+"F2.wireOp",EDGE,"E536.MirrorC"),sQuery(id+"F2.wireOp",EDGE,"E537.MirrorC"),sQuery(id+"F10.wireOp",EDGE,"E578.0"),sQuery(id+"F10.wireOp",EDGE,"E578.1"),sQuery(id+"F10.wireOp",EDGE,"E578.2"),sQuery(id+"F10.wireOp",EDGE,"E578.3")])],"isStart":false});
            var Q1;
            Q1=makeQuery(id+"F11.opExtrude","SWEPT_FACE",FACE,{"disambiguationData":[OSD([sQuery(id+"F10.wireOp",EDGE,"E578.1")])]});
            var Q2;
            Q2=makeQuery(id+"F11.opExtrude","SWEPT_FACE",FACE,{"disambiguationData":[OSD([sQuery(id+"F10.wireOp",EDGE,"E578.2")])]});
            var Q3;
            Q3=makeQuery(id+"F11.opExtrude","SWEPT_FACE",FACE,{"disambiguationData":[OSD([sQuery(id+"F10.wireOp",EDGE,"E578.3")])]});
            var Q4;
            Q4=makeQuery(id+"F11.opExtrude","SWEPT_FACE",FACE,{"disambiguationData":[OSD([sQuery(id+"F10.wireOp",EDGE,"E578.0")])]});
            var Q5;
            Q5=makeQuery(id+"F3.opExtrude","CAP_FACE",FACE,{"disambiguationData":[OSD([sQuery(id+"F2.wireOp",EDGE,"E501.bottom"),sQuery(id+"F2.wireOp",EDGE,"E501.top"),sQuery(id+"F2.wireOp",EDGE,"E501.left"),sQuery(id+"F2.wireOp",EDGE,"E501.right"),sQuery(id+"F2.wireOp",EDGE,"E503.bottom"),sQuery(id+"F2.wireOp",EDGE,"E503.top"),sQuery(id+"F2.wireOp",EDGE,"E503.left"),sQuery(id+"F2.wireOp",EDGE,"E503.right"),sQuery(id+"F2.wireOp",EDGE,"E504.bottom"),sQuery(id+"F2.wireOp",EDGE,"E504.top"),sQuery(id+"F2.wireOp",EDGE,"E504.left"),sQuery(id+"F2.wireOp",EDGE,"E504.right"),sQuery(id+"F2.wireOp",EDGE,"E506"),sQuery(id+"F2.wireOp",EDGE,"E507"),sQuery(id+"F2.wireOp",EDGE,"E508"),sQuery(id+"F2.wireOp",EDGE,"E509"),sQuery(id+"F2.wireOp",EDGE,"E512"),sQuery(id+"F2.wireOp",EDGE,"E513"),sQuery(id+"F2.wireOp",EDGE,"E514"),sQuery(id+"F2.wireOp",EDGE,"E515"),sQuery(id+"F2.wireOp",EDGE,"E519.bottom"),sQuery(id+"F2.wireOp",EDGE,"E519.top"),sQuery(id+"F2.wireOp",EDGE,"E519.left"),sQuery(id+"F2.wireOp",EDGE,"E519.right"),sQuery(id+"F2.wireOp",EDGE,"E522"),sQuery(id+"F2.wireOp",EDGE,"E523.MirrorC"),sQuery(id+"F2.wireOp",EDGE,"E524.MirrorC"),sQuery(id+"F2.wireOp",EDGE,"E525.MirrorC"),sQuery(id+"F2.wireOp",EDGE,"E526.MirrorC"),sQuery(id+"F2.wireOp",EDGE,"E527.MirrorC"),sQuery(id+"F2.wireOp",EDGE,"E528.MirrorC"),sQuery(id+"F2.wireOp",EDGE,"E529.MirrorC"),sQuery(id+"F2.wireOp",EDGE,"E530.MirrorC"),sQuery(id+"F2.wireOp",EDGE,"E531.MirrorC"),sQuery(id+"F2.wireOp",EDGE,"E532.MirrorC"),sQuery(id+"F2.wireOp",EDGE,"E533.MirrorC"),sQuery(id+"F2.wireOp",EDGE,"E534.MirrorC"),sQuery(id+"F2.wireOp",EDGE,"E535.MirrorC"),sQuery(id+"F2.wireOp",EDGE,"E536.MirrorC"),sQuery(id+"F2.wireOp",EDGE,"E537.MirrorC")])],"isStart":false});
            shell(context, id + "F19", {"entities" : qUnion([Q0, Q1, Q2, Q3, Q4, Q5]), "thickness" : 3.3 * mm});
        }
        {
            var Q0;
            Q0=makeQuery(id+"F19.opShell","OFFSET_FACE",FACE,{"disambiguationData":[OSD([sQuery(id+"F2.wireOp",EDGE,"E501.bottom"),sQuery(id+"F2.wireOp",EDGE,"E501.top"),sQuery(id+"F2.wireOp",EDGE,"E501.left"),sQuery(id+"F2.wireOp",EDGE,"E501.right"),sQuery(id+"F2.wireOp",EDGE,"E504.bottom"),sQuery(id+"F2.wireOp",EDGE,"E504.top"),sQuery(id+"F2.wireOp",EDGE,"E504.left"),sQuery(id+"F2.wireOp",EDGE,"E504.right"),sQuery(id+"F2.wireOp",EDGE,"E506"),sQuery(id+"F2.wireOp",EDGE,"E507"),sQuery(id+"F2.wireOp",EDGE,"E508"),sQuery(id+"F2.wireOp",EDGE,"E509"),sQuery(id+"F2.wireOp",EDGE,"E514"),sQuery(id+"F2.wireOp",EDGE,"E515"),sQuery(id+"F2.wireOp",EDGE,"E522"),sQuery(id+"F2.wireOp",EDGE,"E523.MirrorC"),sQuery(id+"F2.wireOp",EDGE,"E524.MirrorC"),sQuery(id+"F2.wireOp",EDGE,"E525.MirrorC"),sQuery(id+"F2.wireOp",EDGE,"E526.MirrorC"),sQuery(id+"F2.wireOp",EDGE,"E527.MirrorC"),sQuery(id+"F2.wireOp",EDGE,"E528.MirrorC"),sQuery(id+"F2.wireOp",EDGE,"E529.MirrorC"),sQuery(id+"F2.wireOp",EDGE,"E530.MirrorC"),sQuery(id+"F2.wireOp",EDGE,"E531.MirrorC"),sQuery(id+"F2.wireOp",EDGE,"E532.MirrorC"),sQuery(id+"F2.wireOp",EDGE,"E533.MirrorC"),sQuery(id+"F2.wireOp",EDGE,"E534.MirrorC"),sQuery(id+"F2.wireOp",EDGE,"E535.MirrorC"),sQuery(id+"F2.wireOp",EDGE,"E536.MirrorC"),sQuery(id+"F2.wireOp",EDGE,"E537.MirrorC"),sQuery(id+"F10.wireOp",EDGE,"E578.0"),sQuery(id+"F10.wireOp",EDGE,"E578.1"),sQuery(id+"F10.wireOp",EDGE,"E578.2"),sQuery(id+"F10.wireOp",EDGE,"E578.3")])]});
            var sketch = newSketch(context, id + "F20", { "sketchPlane" : qUnion([Q0])});
            skPoint(sketch, "E604", {"position": v(-54.56, -25.64) * mm});
            skPoint(sketch, "E605", {"position": v(-54.56, -50.64) * mm});
            skPoint(sketch, "E606", {"position": v(-10.56, -50.64) * mm});
            skPoint(sketch, "E607", {"position": v(-10.56, -25.64) * mm});
            skCircle(sketch, "E608", {"center": v(-54.56, -25.64) * mm, "radius": 1 * mm});
            skCircle(sketch, "E609", {"center": v(-54.56, -50.64) * mm, "radius": 1 * mm});
            skCircle(sketch, "E610", {"center": v(-10.56, -50.64) * mm, "radius": 1 * mm});
            skCircle(sketch, "E611", {"center": v(-10.56, -25.64) * mm, "radius": 1 * mm});
            skSolve(sketch);
        }
        {
            var Q0;
            Q0 = qSketchRegion(id + "F20", true);
            extrude(context, id + "F21", {"entities" : qUnion([Q0]), "oppositeDirection" : true, "depth" : 25 * mm});
        }
        {
            var Q0;
            Q0=makeQuery(id+"F21.opExtrude","SWEPT_FACE",FACE,{"disambiguationData":[OSD([sQuery(id+"F20.wireOp",EDGE,"E609")])]});
            var Q1;
            Q1=makeQuery(id+"F21.opExtrude","SWEPT_FACE",FACE,{"disambiguationData":[OSD([sQuery(id+"F20.wireOp",EDGE,"E610")])]});
            var Q2;
            Q2=makeQuery(id+"F21.opExtrude","SWEPT_FACE",FACE,{"disambiguationData":[OSD([sQuery(id+"F20.wireOp",EDGE,"E611")])]});
            var Q3;
            Q3=makeQuery(id+"F21.opExtrude","SWEPT_FACE",FACE,{"disambiguationData":[OSD([sQuery(id+"F20.wireOp",EDGE,"E608")])]});
            fillet(context, id + "F22", {"entities" : qUnion([Q0, Q1, Q2, Q3]), "radius" : 0.5 * mm, "tangentPropagation" : true, "allowEdgeOverflow" : false});
        }
        {
            var Q0;
            Q0=makeQuery(id+"F5.opExtrude","CAP_FACE",FACE,{"disambiguationData":[OSD([sQuery(id+"F4.wireOp",EDGE,"E538"),sQuery(id+"F4.wireOp",EDGE,"E539"),sQuery(id+"F4.wireOp",EDGE,"E540.13"),sQuery(id+"F4.wireOp",EDGE,"E540.14"),sQuery(id+"F4.wireOp",EDGE,"E549"),sQuery(id+"F4.wireOp",EDGE,"E550"),sQuery(id+"F4.wireOp",EDGE,"E551"),sQuery(id+"F4.wireOp",EDGE,"E552"),sQuery(id+"F4.wireOp",EDGE,"E553"),sQuery(id+"F4.wireOp",EDGE,"E554"),sQuery(id+"F4.wireOp",EDGE,"E555"),sQuery(id+"F4.wireOp",EDGE,"E556"),sQuery(id+"F4.wireOp",EDGE,"E557.bottom"),sQuery(id+"F4.wireOp",EDGE,"E557.top"),sQuery(id+"F4.wireOp",EDGE,"E557.left"),sQuery(id+"F4.wireOp",EDGE,"E557.right"),sQuery(id+"F4.wireOp",EDGE,"E558"),sQuery(id+"F4.wireOp",EDGE,"E564.MirrorC"),sQuery(id+"F4.wireOp",EDGE,"E565.MirrorC"),sQuery(id+"F4.wireOp",EDGE,"E566.MirrorC")])],"isStart":true});
            var sketch = newSketch(context, id + "F23", { "sketchPlane" : qUnion([Q0])});
            skCircle(sketch, "E612.0", {"center": v(-51.22, 20.36) * mm, "radius": 0.97 * mm});
            skCircle(sketch, "E612.1", {"center": v(-48.68, 20.36) * mm, "radius": 0.97 * mm});
            skCircle(sketch, "E612.2", {"center": v(-12.75, 22.35) * mm, "radius": 0.97 * mm});
            skCircle(sketch, "E612.3", {"center": v(-10.2, 22.35) * mm, "radius": 0.97 * mm});
            skCircle(sketch, "E612.4", {"center": v(-10.46, 19.8) * mm, "radius": 0.97 * mm});
            skCircle(sketch, "E612.5", {"center": v(-13, 19.8) * mm, "radius": 0.97 * mm});
            skCircle(sketch, "E612.6", {"center": v(-12.75, 17.27) * mm, "radius": 0.97 * mm});
            skCircle(sketch, "E612.7", {"center": v(-10.2, 17.27) * mm, "radius": 0.97 * mm});
            skCircle(sketch, "E612.8", {"center": v(-10.46, 14.73) * mm, "radius": 0.97 * mm});
            skCircle(sketch, "E612.9", {"center": v(-13, 14.73) * mm, "radius": 0.97 * mm});
            skSolve(sketch);
        }
        {
            var Q0;
            Q0 = qSketchRegion(id + "F23", true);
            extrude(context, id + "F24", {"entities" : qUnion([Q0]), "oppositeDirection" : true, "depth" : 32 * mm});
        }
        {
            var Q0;
            Q0=makeQuery(id+"F11.opExtrude","CAP_FACE",FACE,{"disambiguationData":[OSD([sQuery(id+"F2.wireOp",EDGE,"E501.bottom"),sQuery(id+"F2.wireOp",EDGE,"E501.top"),sQuery(id+"F2.wireOp",EDGE,"E501.left"),sQuery(id+"F2.wireOp",EDGE,"E501.right"),sQuery(id+"F2.wireOp",EDGE,"E504.bottom"),sQuery(id+"F2.wireOp",EDGE,"E504.top"),sQuery(id+"F2.wireOp",EDGE,"E504.left"),sQuery(id+"F2.wireOp",EDGE,"E504.right"),sQuery(id+"F2.wireOp",EDGE,"E506"),sQuery(id+"F2.wireOp",EDGE,"E507"),sQuery(id+"F2.wireOp",EDGE,"E508"),sQuery(id+"F2.wireOp",EDGE,"E509"),sQuery(id+"F2.wireOp",EDGE,"E514"),sQuery(id+"F2.wireOp",EDGE,"E515"),sQuery(id+"F2.wireOp",EDGE,"E522"),sQuery(id+"F2.wireOp",EDGE,"E523.MirrorC"),sQuery(id+"F2.wireOp",EDGE,"E524.MirrorC"),sQuery(id+"F2.wireOp",EDGE,"E525.MirrorC"),sQuery(id+"F2.wireOp",EDGE,"E526.MirrorC"),sQuery(id+"F2.wireOp",EDGE,"E527.MirrorC"),sQuery(id+"F2.wireOp",EDGE,"E528.MirrorC"),sQuery(id+"F2.wireOp",EDGE,"E529.MirrorC"),sQuery(id+"F2.wireOp",EDGE,"E530.MirrorC"),sQuery(id+"F2.wireOp",EDGE,"E531.MirrorC"),sQuery(id+"F2.wireOp",EDGE,"E532.MirrorC"),sQuery(id+"F2.wireOp",EDGE,"E533.MirrorC"),sQuery(id+"F2.wireOp",EDGE,"E534.MirrorC"),sQuery(id+"F2.wireOp",EDGE,"E535.MirrorC"),sQuery(id+"F2.wireOp",EDGE,"E536.MirrorC"),sQuery(id+"F2.wireOp",EDGE,"E537.MirrorC"),sQuery(id+"F10.wireOp",EDGE,"E578.0"),sQuery(id+"F10.wireOp",EDGE,"E578.1"),sQuery(id+"F10.wireOp",EDGE,"E578.2"),sQuery(id+"F10.wireOp",EDGE,"E578.3")])],"isStart":false});
            var sketch = newSketch(context, id + "F25", { "sketchPlane" : qUnion([Q0])});
            skLineSegment(sketch, "E613.0", {"start": v(-66.57, 11.36) * mm, "end": v(-67.26, 10.17) * mm});
            skLineSegment(sketch, "E613.1", {"start": v(-66.57, 11.36) * mm, "end": v(-67.26, 12.55) * mm});
            skLineSegment(sketch, "E613.2", {"start": v(-67.26, 10.17) * mm, "end": v(-67.26, 12.55) * mm});
            skLineSegment(sketch, "E614.0", {"start": v(-54.46, 18.11) * mm, "end": v(-53.74, 16.85) * mm});
            skLineSegment(sketch, "E614.1", {"start": v(-54.65, 18.11) * mm, "end": v(-55.37, 16.85) * mm});
            skArc(sketch, "E614.2", {"start": v(-54.73, 18.26) * mm, "mid": v(-54.56, 18.26) * mm, "end": v(-54.38, 18.26) * mm});
            skArc(sketch, "E614.3", {"start": v(-55.37, 16.85) * mm, "mid": v(-54.56, 16.91) * mm, "end": v(-53.74, 16.85) * mm});
            skLineSegment(sketch, "E615.0", {"start": v(-54.38, 18.26) * mm, "end": v(-54.46, 18.11) * mm});
            skLineSegment(sketch, "E615.1", {"start": v(-54.73, 18.26) * mm, "end": v(-54.65, 18.11) * mm});
            skPoint(sketch, "E616.orphan", {"position": v(-50.6, 24.81) * mm});
            skPoint(sketch, "E617.orphan", {"position": v(-58.51, 24.81) * mm});
            skLineSegment(sketch, "E618.0", {"start": v(-54.38, 4.47) * mm, "end": v(-54.46, 4.61) * mm});
            skPoint(sketch, "E619.0", {"position": v(-54.1, 5.24) * mm});
            skArc(sketch, "E620.0", {"start": v(-53.74, 5.87) * mm, "mid": v(-54.56, 5.81) * mm, "end": v(-55.37, 5.87) * mm});
            skLineSegment(sketch, "E621.0", {"start": v(-54.65, 4.61) * mm, "end": v(-55.37, 5.87) * mm});
            skLineSegment(sketch, "E622.0", {"start": v(-54.73, 4.47) * mm, "end": v(-54.65, 4.61) * mm});
            skArc(sketch, "E623.0", {"start": v(-54.38, 4.47) * mm, "mid": v(-54.56, 4.46) * mm, "end": v(-54.73, 4.47) * mm});
            skPoint(sketch, "E624.orphan", {"position": v(-50.51, -2.24) * mm});
            skPoint(sketch, "E625.orphan", {"position": v(-58.6, -2.24) * mm});
            skSolve(sketch);
        }
        {
            var Q0;
            Q0=makeQuery(id+"F25.imprint","IMPRINT",FACE,{"disambiguationData":[TD([[makeQuery(id+"F25.imprint","IMPRINT",EDGE,{"derivedFrom":sQuery(id+"F25.wireOp",EDGE,"E618.0")}),1.0]])]});
            var Q1;
            Q1=makeQuery(id+"F25.imprint","IMPRINT",FACE,{"disambiguationData":[TD([[makeQuery(id+"F25.imprint","IMPRINT",EDGE,{"derivedFrom":sQuery(id+"F25.wireOp",EDGE,"E613.0")}),-1.0]])]});
            var Q2;
            Q2=makeQuery(id+"F25.imprint","IMPRINT",FACE,{"disambiguationData":[TD([[makeQuery(id+"F25.imprint","IMPRINT",EDGE,{"derivedFrom":sQuery(id+"F25.wireOp",EDGE,"E614.0")}),-1.0]])]});
            extrude(context, id + "F26", {"entities" : qUnion([Q0, Q1, Q2]), "operationType" : NewBodyOperationType.ADD, "endBound" : BoundingType.UP_TO_NEXT, "oppositeDirection" : true, "depth" : 25 * mm});
        }
    });
